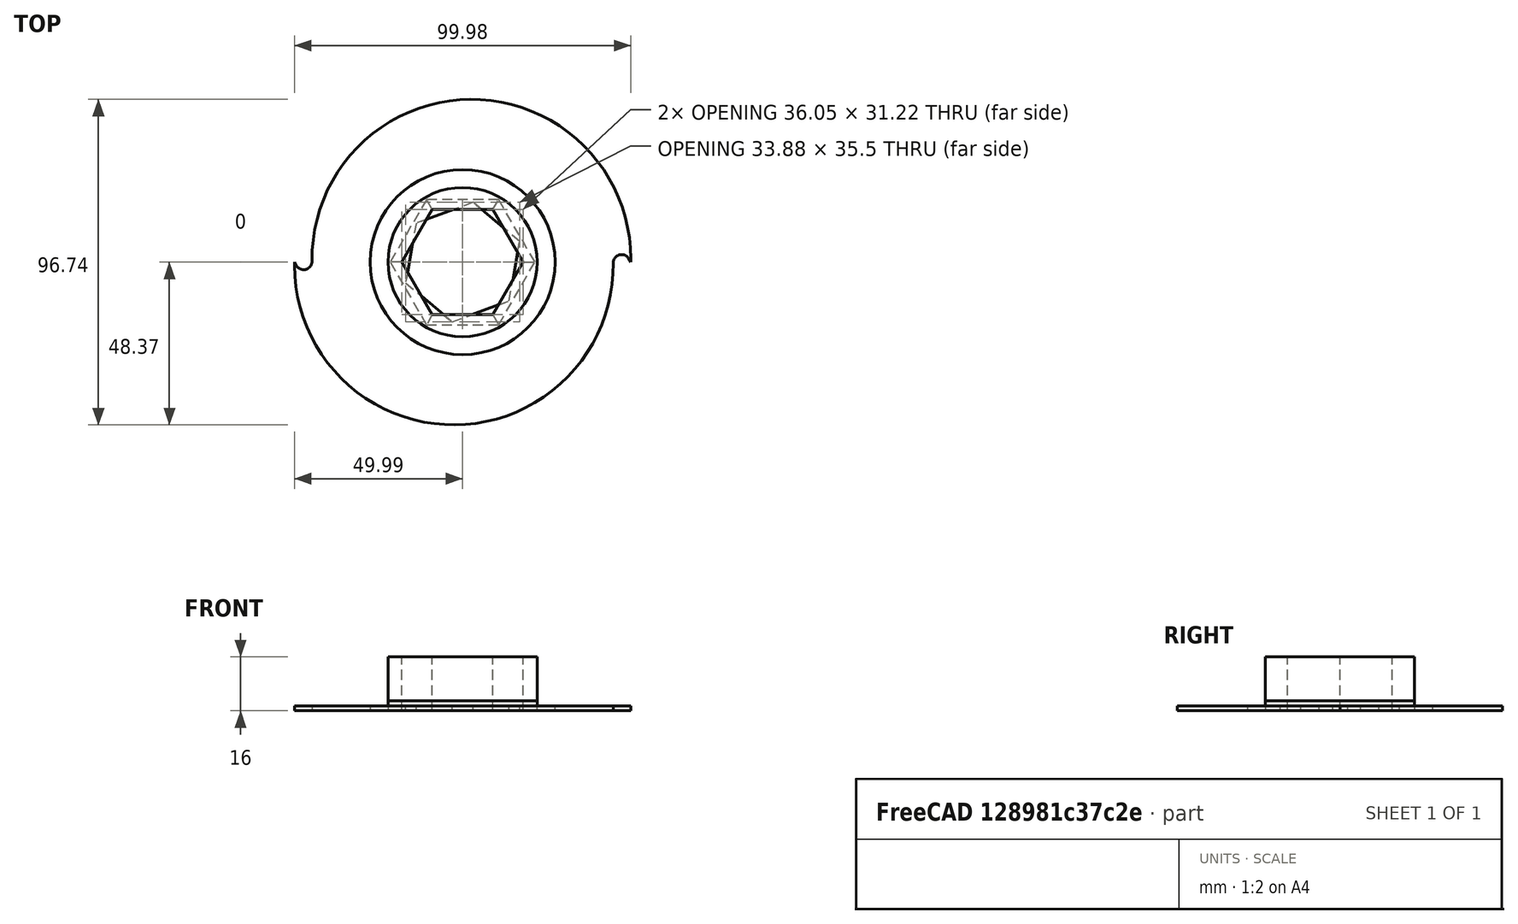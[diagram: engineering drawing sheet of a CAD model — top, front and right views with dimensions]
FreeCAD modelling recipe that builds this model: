
FCSTD DOCUMENT  (FreeCAD 0.21R33675 (Git))
Label: recicladora_cuchillas
License: All rights reserved
LicenseURL: https://en.wikipedia.org/wiki/All_rights_reserved
objects: Sketcher::SketchObject×21, PartDesign::CoordinateSystem×18, TechDraw::DrawViewDimension×13, PartDesign::Pad×9, PartDesign::Body×9, TechDraw::DrawProjGroupItem×8, TechDraw::DrawProjGroup×7, App::FeaturePython×1, PartDesign::Chamfer×1, TechDraw::DrawSVGTemplate×1, TechDraw::DrawPage×1
note: 74 computed .brp shape members not serialized (recipe doc carries the construction recipe); baked Part::Feature solids carry a one-line shape summary decoded from their .brp

FEATURE [Sketcher::SketchObject] Sketch001
  FullyConstrained = true
  MapMode = 5
  Support = -> [XY_Plane001]
  expr: Constraints[0] = dd.ddDiamteroExterno
  expr: Constraints[13] = dd.ddLargoPunta
  expr: Constraints[14] = dd.ddRadioMenor
  expr: Constraints[33] = dd.ddDistanceHexagono
  expr: Constraints[36] = dd.ddAngulo1
  expr: Constraints[8] = dd.ddAnguloPunta
  expr: Constraints[9] = dd.ddAnguloPunta
  sketch-geometry (17):
    g0: Circle CenterX=0 CenterY=0 CenterZ=0 NormalX=0 NormalY=0 NormalZ=1 AngleXU=0 Radius=50
    g1: LineSegment StartX=49.99 StartY=0 StartZ=0 EndX=49.99 EndY=1 EndZ=0
    g2: LineSegment StartX=49.99 StartY=0 StartZ=0 EndX=49.4126 EndY=1 EndZ=0
    g3: ArcOfCircle CenterX=2.61839 CenterY=1 CenterZ=0 NormalX=0 NormalY=0 NormalZ=1 AngleXU=0 Radius=47.3716 StartAngle=0 EndAngle=3.15663
    g4: ArcOfCircle CenterX=-2.61839 CenterY=-1 CenterZ=0 NormalX=0 NormalY=0 NormalZ=1 AngleXU=0 Radius=47.3716 StartAngle=3.14159 EndAngle=6.29822
    g5: LineSegment StartX=-49.99 StartY=0 StartZ=0 EndX=-49.99 EndY=-1 EndZ=0
    g6: LineSegment StartX=-49.99 StartY=0 StartZ=0 EndX=-49.4126 EndY=-1 EndZ=0
    g7: ArcOfCircle CenterX=-47.2476 CenterY=0.25 CenterZ=0 NormalX=0 NormalY=0 NormalZ=1 AngleXU=0 Radius=2.5 StartAngle=3.66519 EndAngle=6.29822
    g8: ArcOfCircle CenterX=47.2476 CenterY=-0.25 CenterZ=0 NormalX=0 NormalY=0 NormalZ=1 AngleXU=0 Radius=2.5 StartAngle=0.523599 EndAngle=3.15663
    g9: LineSegment StartX=-9.01244 StartY=-15.61 StartZ=0 EndX=9.01244 EndY=-15.61 EndZ=0
    g10: LineSegment StartX=9.01244 StartY=-15.61 StartZ=0 EndX=18.0249 EndY=0 EndZ=0
    g11: LineSegment StartX=18.0249 StartY=0 StartZ=0 EndX=9.01244 EndY=15.61 EndZ=0
    g12: LineSegment StartX=9.01244 StartY=15.61 StartZ=0 EndX=-9.01244 EndY=15.61 EndZ=0
    g13: LineSegment StartX=-9.01244 StartY=15.61 StartZ=0 EndX=-18.0249 EndY=1.8e-15 EndZ=0
    g14: LineSegment StartX=-18.0249 StartY=2e-15 StartZ=0 EndX=-9.01244 EndY=-15.61 EndZ=0
    g15: Circle CenterX=0 CenterY=0 CenterZ=0 NormalX=0 NormalY=0 NormalZ=1 AngleXU=0 Radius=18.0249
    g16: LineSegment StartX=0 StartY=0 StartZ=0 EndX=18.0249 EndY=0 EndZ=0
  constraints (42):
    c: Diameter(g0) = 100
    c: Tangent(g3,g1) = -1.5708
    c: Coincident(g6,g5)
    c: Tangent(g7,g6) = -1.5708
    c: Tangent(g7,g3) = 1.5708
    c: Tangent(g8,g2) = -1.5708
    c: Tangent(g8,g4) = 1.5708
    c: Coincident(g0,g-1)
    c: Angle(g1,g2) = 0.523599
    c: Angle(g5,g6) = 0.523599
    c: PointOnObject(g4,g0)
    c: Equal(g7,g8)
    c: Equal(g3,g4)
    c: Distance(g1) = 1
    c: Radius(g8) = 2.5
    c: Coincident(g9,g10)
    c: Coincident(g10,g11)
    c: Coincident(g11,g12)
    c: Coincident(g12,g13)
    c: Coincident(g13,g14)
    c: Coincident(g14,g9)
    c: Equal(g9, g10-g14) x5
    c: PointOnObject(g9,g15)
    c: PointOnObject(g10,g15)
    c: PointOnObject(g11,g15)
    c: PointOnObject(g12,g15)
    c: PointOnObject(g13,g15)
    c: PointOnObject(g14,g15)
    c: Coincident(g15,g0)
    c: Distance(g9,g10) = 31.22
    c: Coincident(g16,g0)
    c: Coincident(g16,g10)
    c: Angle(g-1,g16) = 0
    c: Tangent(g4,g5) = -1.5708
    c: Vertical(g1)
    c: Coincident(g1,g2)
    c: PointOnObject(g1,g0)
    c: PointOnObject(g1,g-1)
    c: Horizontal(g2,g1)
    c: Vertical(g5)
    c: PointOnObject(g5,g-1)
    c: Horizontal(g6,g4)
FEATURE [App::FeaturePython] dd  label="ddCuchillas"  # WARN: FeaturePython — macro-defined, semantics opaque (R4)
  DynamicData = Created with DynamicData (v2.46) workbench. | This is a simple container object built | for holding custom properties.
  ddAngulo1 = 0
  ddAngulo2 = 10
  ddAngulo3 = 20
  ddAngulo4 = 30
  ddAngulo5 = 40
  ddAngulo6 = 50
  ddAnguloPunta = 30
  ddDiametroSeparador = 55
  ddDiamteroExterno = 100
  ddDistanceHexagono = 31.22
  ddGrosorPlaca = 1.5
  ddLargoPunta = 1
  ddRadioMenor = 2.5
  expr: ddRadioMenor = 2.5
FEATURE [PartDesign::Pad] Pad001
  Direction = (0,0,1)
  Length = 1.5
  Length2 = 10
  Profile = -> Sketch001
  Type = 0
  expr: Length = <<ddCuchillas>>.ddGrosorPlaca
FEATURE [Sketcher::SketchObject] Sketch
  FullyConstrained = true
  MapMode = 5
  Placement = pos=(0,0,1.5) rot=(0,0,1;0rad)
  Support = -> [Pad001]
  expr: Constraints[0] = Sketch001.Constraints[0]
  expr: Constraints[14] = Sketch001.Constraints[8]
  expr: Constraints[15] = Sketch001.Constraints[9]
  expr: Constraints[21] = Sketch001.Constraints[13]
  expr: Constraints[22] = Sketch001.Constraints[14]
  expr: Constraints[41] = Sketch001.Constraints[33]
  expr: Constraints[44] = Sketch001.Constraints[36]
  sketch-geometry (17):
    g0: Circle CenterX=0 CenterY=0 CenterZ=0 NormalX=0 NormalY=0 NormalZ=1 AngleXU=0 Radius=50
    g1: LineSegment StartX=50 StartY=0 StartZ=0 EndX=49.99 EndY=0.99995 EndZ=0
    g2: LineSegment StartX=50 StartY=0 StartZ=0 EndX=49.4914 EndY=0.860982 EndZ=0
    g3: ArcOfCircle CenterX=2.57666 CenterY=0.525793 CenterZ=0 NormalX=0 NormalY=0 NormalZ=1 AngleXU=0 Radius=47.4157 StartAngle=0.0100002 EndAngle=3.1439
    g4: ArcOfCircle CenterX=-2.57666 CenterY=-0.525793 CenterZ=0 NormalX=0 NormalY=0 NormalZ=1 AngleXU=0 Radius=47.4157 StartAngle=3.15159 EndAngle=6.28549
    g5: LineSegment StartX=-50 StartY=0 StartZ=0 EndX=-49.99 EndY=-0.99995 EndZ=0
    g6: LineSegment StartX=-50 StartY=0 StartZ=0 EndX=-49.4914 EndY=-0.860982 EndZ=0
    g7: ArcOfCircle CenterX=-47.3389 CenterY=0.410606 CenterZ=0 NormalX=0 NormalY=0 NormalZ=1 AngleXU=0 Radius=2.5 StartAngle=3.67519 EndAngle=6.28549
    g8: ArcOfCircle CenterX=47.3389 CenterY=-0.410606 CenterZ=0 NormalX=0 NormalY=0 NormalZ=1 AngleXU=0 Radius=2.5 StartAngle=0.533599 EndAngle=3.1439
    g9: LineSegment StartX=-9.01244 StartY=-15.61 StartZ=0 EndX=9.01244 EndY=-15.61 EndZ=0
    g10: LineSegment StartX=9.01244 StartY=-15.61 StartZ=0 EndX=18.0249 EndY=0 EndZ=0
    g11: LineSegment StartX=18.0249 StartY=0 StartZ=0 EndX=9.01244 EndY=15.61 EndZ=0
    g12: LineSegment StartX=9.01244 StartY=15.61 StartZ=0 EndX=-9.01244 EndY=15.61 EndZ=0
    g13: LineSegment StartX=-9.01244 StartY=15.61 StartZ=0 EndX=-18.0249 EndY=0 EndZ=0
    g14: LineSegment StartX=-18.0249 StartY=7e-16 StartZ=0 EndX=-9.01244 EndY=-15.61 EndZ=0
    g15: Circle CenterX=0 CenterY=0 CenterZ=0 NormalX=0 NormalY=0 NormalZ=1 AngleXU=0 Radius=18.0249
    g16: LineSegment StartX=0 StartY=0 StartZ=0 EndX=18.0249 EndY=0 EndZ=0
  constraints (42):
    c: Diameter(g0) = 100
    c: PointOnObject(g1,g0)
    c: Coincident(g2,g1)
    c: PointOnObject(g1,g-1)
    c: Tangent(g3,g1) = -1.5708
    c: PointOnObject(g5,g-1)
    c: Coincident(g6,g5)
    c: Tangent(g7,g6) = -1.5708
    c: Tangent(g7,g3) = 1.5708
    c: Tangent(g8,g2) = -1.5708
    c: Tangent(g8,g4) = 1.5708
    c: PointOnObject(g5,g0)
    c: Coincident(g0,g-1)
    c: PointOnObject(g1,g0)
    c: Angle(g1,g2) = 0.523599
    c: Angle(g5,g6) = 0.523599
    c: Equal(g5,g1)
    c: PointOnObject(g4,g0)
    c: Equal(g7,g8)
    c: Equal(g3,g4)
    c: Equal(g5,g6)
    c: Distance(g1) = 1
    c: Radius(g8) = 2.5
    c: Coincident(g9,g10)
    c: Coincident(g10,g11)
    c: Coincident(g11,g12)
    c: Coincident(g12,g13)
    c: Coincident(g13,g14)
    c: Coincident(g14,g9)
    c: Equal(g9, g10-g14) x5
    c: PointOnObject(g9,g15)
    c: PointOnObject(g10,g15)
    c: PointOnObject(g11,g15)
    c: PointOnObject(g12,g15)
    c: PointOnObject(g13,g15)
    c: PointOnObject(g14,g15)
    c: Coincident(g15,g0)
    c: Distance(g9,g10) = 31.22
    c: Coincident(g16,g0)
    c: Coincident(g16,g10)
    c: Angle(g-1,g16) = 0
    c: Tangent(g4,g5) = -1.5708
FEATURE [Sketcher::SketchObject] Sketch002
  FullyConstrained = true
  MapMode = 5
  Placement = pos=(0,0,0) rot=(1,0,0;3.14159rad)
  Support = -> [Pad001]
  expr: Constraints[0] = Sketch.Constraints[0]
  expr: Constraints[14] = Sketch.Constraints[14]
  expr: Constraints[15] = Sketch.Constraints[15]
  expr: Constraints[21] = Sketch.Constraints[21]
  expr: Constraints[22] = Sketch.Constraints[22]
  expr: Constraints[41] = Sketch.Constraints[41]
  expr: Constraints[44] = Sketch.Constraints[44]
  sketch-geometry (17):
    g0: Circle CenterX=0 CenterY=0 CenterZ=0 NormalX=0 NormalY=0 NormalZ=1 AngleXU=0 Radius=50
    g1: LineSegment StartX=50 StartY=0 StartZ=0 EndX=49.99 EndY=0.99995 EndZ=0
    g2: LineSegment StartX=50 StartY=0 StartZ=0 EndX=49.4914 EndY=0.860982 EndZ=0
    g3: ArcOfCircle CenterX=2.57666 CenterY=0.525793 CenterZ=0 NormalX=0 NormalY=0 NormalZ=1 AngleXU=0 Radius=47.4157 StartAngle=0.0100002 EndAngle=3.1439
    g4: ArcOfCircle CenterX=-2.57666 CenterY=-0.525793 CenterZ=0 NormalX=0 NormalY=0 NormalZ=1 AngleXU=0 Radius=47.4157 StartAngle=3.15159 EndAngle=6.28549
    g5: LineSegment StartX=-50 StartY=0 StartZ=0 EndX=-49.99 EndY=-0.99995 EndZ=0
    g6: LineSegment StartX=-50 StartY=0 StartZ=0 EndX=-49.4914 EndY=-0.860982 EndZ=0
    g7: ArcOfCircle CenterX=-47.3389 CenterY=0.410606 CenterZ=0 NormalX=0 NormalY=0 NormalZ=1 AngleXU=0 Radius=2.5 StartAngle=3.67519 EndAngle=6.28549
    g8: ArcOfCircle CenterX=47.3389 CenterY=-0.410606 CenterZ=0 NormalX=0 NormalY=0 NormalZ=1 AngleXU=0 Radius=2.5 StartAngle=0.533599 EndAngle=3.1439
    g9: LineSegment StartX=-9.01244 StartY=-15.61 StartZ=0 EndX=9.01244 EndY=-15.61 EndZ=0
    g10: LineSegment StartX=9.01244 StartY=-15.61 StartZ=0 EndX=18.0249 EndY=0 EndZ=0
    g11: LineSegment StartX=18.0249 StartY=0 StartZ=0 EndX=9.01244 EndY=15.61 EndZ=0
    g12: LineSegment StartX=9.01244 StartY=15.61 StartZ=0 EndX=-9.01244 EndY=15.61 EndZ=0
    g13: LineSegment StartX=-9.01244 StartY=15.61 StartZ=0 EndX=-18.0249 EndY=1.8e-15 EndZ=0
    g14: LineSegment StartX=-18.0249 StartY=2.1e-15 StartZ=0 EndX=-9.01244 EndY=-15.61 EndZ=0
    g15: Circle CenterX=0 CenterY=0 CenterZ=0 NormalX=0 NormalY=0 NormalZ=1 AngleXU=0 Radius=18.0249
    g16: LineSegment StartX=0 StartY=0 StartZ=0 EndX=18.0249 EndY=0 EndZ=0
  constraints (42):
    c: Diameter(g0) = 100
    c: PointOnObject(g1,g0)
    c: Coincident(g2,g1)
    c: PointOnObject(g1,g-1)
    c: Tangent(g3,g1) = -1.5708
    c: PointOnObject(g5,g-1)
    c: Coincident(g6,g5)
    c: Tangent(g7,g6) = -1.5708
    c: Tangent(g7,g3) = 1.5708
    c: Tangent(g8,g2) = -1.5708
    c: Tangent(g8,g4) = 1.5708
    c: PointOnObject(g5,g0)
    c: Coincident(g0,g-1)
    c: PointOnObject(g1,g0)
    c: Angle(g1,g2) = 0.523599
    c: Angle(g5,g6) = 0.523599
    c: Equal(g5,g1)
    c: PointOnObject(g4,g0)
    c: Equal(g7,g8)
    c: Equal(g3,g4)
    c: Equal(g5,g6)
    c: Distance(g1) = 1
    c: Radius(g8) = 2.5
    c: Coincident(g9,g10)
    c: Coincident(g10,g11)
    c: Coincident(g11,g12)
    c: Coincident(g12,g13)
    c: Coincident(g13,g14)
    c: Coincident(g14,g9)
    c: Equal(g9, g10-g14) x5
    c: PointOnObject(g9,g15)
    c: PointOnObject(g10,g15)
    c: PointOnObject(g11,g15)
    c: PointOnObject(g12,g15)
    c: PointOnObject(g13,g15)
    c: PointOnObject(g14,g15)
    c: Coincident(g15,g0)
    c: Distance(g9,g10) = 31.22
    c: Coincident(g16,g0)
    c: Coincident(g16,g10)
    c: Angle(g-1,g16) = 0
    c: Tangent(g4,g5) = -1.5708
FEATURE [PartDesign::CoordinateSystem] LCS_cuchilla_entrada
  AttacherType = Attacher::AttachEngine3D
  MapMode = 11
  Placement = pos=(-3.6e-15,0,0) rot=(0,0,1;1.5708rad)
  Support = -> [Sketch002,Pad001]
FEATURE [PartDesign::CoordinateSystem] LCS_cuchilla_salida
  AttacherType = Attacher::AttachEngine3D
  MapMode = 11
  Placement = pos=(-3.6e-15,0,1.5) rot=(0,0,1;1.5708rad)
  Support = -> [Sketch,Pad001]
FEATURE [PartDesign::Body] Body001  label="Cuchilla001"
  Group = -> [Sketch001,Pad001,LCS_cuchilla_entrada,Sketch,Sketch002,LCS_cuchilla_salida]
  Origin = -> Origin001
  Tip = -> Pad001
FEATURE [Sketcher::SketchObject] Sketch018
  FullyConstrained = true
  MapMode = 5
  Support = -> [XY_Plane001]
  expr: Constraints[19] = 22.18 * 2
  expr: Constraints[20] = dd.ddDistanceHexagono
  sketch-geometry (8):
    g0: LineSegment StartX=9.01244 StartY=15.61 StartZ=0 EndX=-9.01244 EndY=15.61 EndZ=0
    g1: LineSegment StartX=-9.01244 StartY=15.61 StartZ=0 EndX=-18.0249 EndY=-1.8e-15 EndZ=0
    g2: LineSegment StartX=-18.0249 StartY=-1.8e-15 StartZ=0 EndX=-9.01244 EndY=-15.61 EndZ=0
    g3: LineSegment StartX=-9.01244 StartY=-15.61 StartZ=0 EndX=9.01244 EndY=-15.61 EndZ=0
    g4: LineSegment StartX=9.01244 StartY=-15.61 StartZ=0 EndX=18.0249 EndY=0 EndZ=0
    g5: LineSegment StartX=18.0249 StartY=0 StartZ=0 EndX=9.01244 EndY=15.61 EndZ=0
    g6: Circle CenterX=0 CenterY=0 CenterZ=0 NormalX=0 NormalY=0 NormalZ=1 AngleXU=0 Radius=18.0249
    g7: Circle CenterX=0 CenterY=0 CenterZ=0 NormalX=0 NormalY=0 NormalZ=1 AngleXU=0 Radius=22.18
  constraints (18):
    c: Coincident(g0,g1)
    c: Coincident(g1,g2)
    c: Coincident(g2,g3)
    c: Coincident(g3,g4)
    c: Coincident(g4,g5)
    c: Coincident(g5,g0)
    c: Equal(g0, g1-g5) x5
    c: PointOnObject(g0,g6)
    c: PointOnObject(g1,g6)
    c: PointOnObject(g2,g6)
    c: PointOnObject(g3,g6)
    c: PointOnObject(g4,g6)
    c: PointOnObject(g5,g6)
    c: Coincident(g6,g-1)
    c: Coincident(g7,g6)
    c: Diameter(g7) = 44.36
    c: Distance(g1,g0) = 31.22
    c: PointOnObject(g4,g-1)
FEATURE [PartDesign::Pad] Pad007
  Direction = (0,0,1)
  Length = 3
  Length2 = 10
  Profile = -> Sketch018
  Type = 0
FEATURE [PartDesign::Chamfer] Chamfer
  Angle = 45
  Base = -> Pad007 [Edge15,Edge18,Edge20,Edge6,Edge9,Edge12]
  BaseFeature = -> Pad007
  ChamferType = 0
  FlipDirection = false
  Size = 2.9999
  Size2 = 1
  SupportTransform = false
  UseAllEdges = false
  expr: Size = 3 mm - 0.0001 mm
FEATURE [PartDesign::CoordinateSystem] LCS_separador_entrada  label="LCS_separador_inicial_entrada"
  AttacherType = Attacher::AttachEngine3D
  MapMode = 11
  Placement = pos=(-3.6e-15,0,0) rot=(0,0,1;1.5708rad)
  Support = -> [Chamfer]
FEATURE [PartDesign::CoordinateSystem] LCS_separador_inicial_salida
  AttacherType = Attacher::AttachEngine3D
  MapMode = 11
  Placement = pos=(-3.6e-15,0,3) rot=(0,0,1;1.5708rad)
  Support = -> [Chamfer]
FEATURE [PartDesign::Body] Body007  label="SeparadorCuchillaInicial"
  Group = -> [Sketch018,Pad007,Chamfer,LCS_separador_entrada,LCS_separador_inicial_salida]
  Origin = -> Origin007
  Tip = -> Chamfer
FEATURE [Sketcher::SketchObject] Sketch019
  FullyConstrained = true
  MapMode = 5
  Support = -> [XY_Plane001]
  expr: Constraints[19] = <<ddCuchillas>>.ddDiametroSeparador
  expr: Constraints[21] = dd.ddDistanceHexagono
  sketch-geometry (8):
    g0: LineSegment StartX=9.01244 StartY=15.61 StartZ=0 EndX=-9.01244 EndY=15.61 EndZ=0
    g1: LineSegment StartX=-9.01244 StartY=15.61 StartZ=0 EndX=-18.0249 EndY=3.6e-15 EndZ=0
    g2: LineSegment StartX=-18.0249 StartY=3.6e-15 StartZ=0 EndX=-9.01244 EndY=-15.61 EndZ=0
    g3: LineSegment StartX=-9.01244 StartY=-15.61 StartZ=0 EndX=9.01244 EndY=-15.61 EndZ=0
    g4: LineSegment StartX=9.01244 StartY=-15.61 StartZ=0 EndX=18.0249 EndY=0 EndZ=0
    g5: LineSegment StartX=18.0249 StartY=0 StartZ=0 EndX=9.01244 EndY=15.61 EndZ=0
    g6: Circle CenterX=0 CenterY=0 CenterZ=0 NormalX=0 NormalY=0 NormalZ=1 AngleXU=0 Radius=18.0249
    g7: Circle CenterX=0 CenterY=0 CenterZ=0 NormalX=0 NormalY=0 NormalZ=1 AngleXU=0 Radius=27.5
  constraints (18):
    c: Coincident(g0,g1)
    c: Coincident(g1,g2)
    c: Coincident(g2,g3)
    c: Coincident(g3,g4)
    c: Coincident(g4,g5)
    c: Coincident(g5,g0)
    c: Equal(g0, g1-g5) x5
    c: PointOnObject(g0,g6)
    c: PointOnObject(g1,g6)
    c: PointOnObject(g2,g6)
    c: PointOnObject(g3,g6)
    c: PointOnObject(g4,g6)
    c: PointOnObject(g5,g6)
    c: Coincident(g6,g-1)
    c: Coincident(g7,g6)
    c: Diameter(g7) = 55
    c: PointOnObject(g4,g-1)
    c: Distance(g0,g1) = 31.22
FEATURE [PartDesign::Pad] Pad008
  Direction = (0,0,1)
  Length = 1.5
  Length2 = 10
  Profile = -> Sketch019
  Type = 0
  expr: Length = dd.ddGrosorPlaca
FEATURE [PartDesign::CoordinateSystem] LCS_separador  label="LCS_separador_entrada"
  AttacherType = Attacher::AttachEngine3D
  MapMode = 11
  Placement = pos=(0,0,1.5) rot=(0.707107,-0.707107,0;3.14159rad)
  Support = -> [Pad008]
FEATURE [PartDesign::CoordinateSystem] LCS_separador_salida
  AttacherType = Attacher::AttachEngine3D
  MapMode = 11
  Placement = pos=(0,0,0) rot=(0.707107,-0.707107,0;3.14159rad)
  Support = -> [Pad008]
FEATURE [PartDesign::Body] Body008  label="SeparadorCuchilla"
  Group = -> [Sketch019,Pad008,LCS_separador,LCS_separador_salida]
  Origin = -> Origin008
  Tip = -> Pad008
FEATURE [Sketcher::SketchObject] Sketch021
  FullyConstrained = true
  MapMode = 5
  Support = -> [XY_Plane002]
  expr: Constraints[0] = dd.ddDiamteroExterno
  expr: Constraints[13] = dd.ddLargoPunta
  expr: Constraints[14] = dd.ddRadioMenor
  expr: Constraints[33] = dd.ddDistanceHexagono
  expr: Constraints[36] = dd.ddAngulo2
  expr: Constraints[8] = dd.ddAnguloPunta
  expr: Constraints[9] = dd.ddAnguloPunta
  sketch-geometry (17):
    g0: Circle CenterX=0 CenterY=0 CenterZ=0 NormalX=0 NormalY=0 NormalZ=1 AngleXU=0 Radius=50
    g1: LineSegment StartX=49.99 StartY=0 StartZ=0 EndX=49.99 EndY=1 EndZ=0
    g2: LineSegment StartX=49.99 StartY=0 StartZ=0 EndX=49.4126 EndY=1 EndZ=0
    g3: ArcOfCircle CenterX=2.61839 CenterY=1 CenterZ=0 NormalX=0 NormalY=0 NormalZ=1 AngleXU=0 Radius=47.3716 StartAngle=0 EndAngle=3.15663
    g4: ArcOfCircle CenterX=-2.61839 CenterY=-1 CenterZ=0 NormalX=0 NormalY=0 NormalZ=1 AngleXU=0 Radius=47.3716 StartAngle=3.14159 EndAngle=6.29822
    g5: LineSegment StartX=-49.99 StartY=0 StartZ=0 EndX=-49.99 EndY=-1 EndZ=0
    g6: LineSegment StartX=-49.99 StartY=0 StartZ=0 EndX=-49.4126 EndY=-1 EndZ=0
    g7: ArcOfCircle CenterX=-47.2476 CenterY=0.25 CenterZ=0 NormalX=0 NormalY=0 NormalZ=1 AngleXU=0 Radius=2.5 StartAngle=3.66519 EndAngle=6.29822
    g8: ArcOfCircle CenterX=47.2476 CenterY=-0.25 CenterZ=0 NormalX=0 NormalY=0 NormalZ=1 AngleXU=0 Radius=2.5 StartAngle=0.523599 EndAngle=3.15663
    g9: LineSegment StartX=-6.16487 StartY=-16.9378 StartZ=0 EndX=11.5862 EndY=-13.8079 EndZ=0
    g10: LineSegment StartX=11.5862 StartY=-13.8079 StartZ=0 EndX=17.751 EndY=3.12999 EndZ=0
    g11: LineSegment StartX=17.751 StartY=3.12999 StartZ=0 EndX=6.16487 EndY=16.9378 EndZ=0
    g12: LineSegment StartX=6.16487 StartY=16.9378 StartZ=0 EndX=-11.5862 EndY=13.8079 EndZ=0
    g13: LineSegment StartX=-11.5862 StartY=13.8079 StartZ=0 EndX=-17.751 EndY=-3.12999 EndZ=0
    g14: LineSegment StartX=-17.751 StartY=-3.12999 StartZ=0 EndX=-6.16487 EndY=-16.9378 EndZ=0
    g15: Circle CenterX=0 CenterY=0 CenterZ=0 NormalX=0 NormalY=0 NormalZ=1 AngleXU=0 Radius=18.0249
    g16: LineSegment StartX=0 StartY=0 StartZ=0 EndX=17.751 EndY=3.12999 EndZ=0
  constraints (42):
    c: Diameter(g0) = 100
    c: Tangent(g3,g1) = -1.5708
    c: Coincident(g6,g5)
    c: Tangent(g7,g6) = -1.5708
    c: Tangent(g7,g3) = 1.5708
    c: Tangent(g8,g2) = -1.5708
    c: Tangent(g8,g4) = 1.5708
    c: Coincident(g0,g-1)
    c: Angle(g1,g2) = 0.523599
    c: Angle(g5,g6) = 0.523599
    c: PointOnObject(g4,g0)
    c: Equal(g7,g8)
    c: Equal(g3,g4)
    c: Distance(g1) = 1
    c: Radius(g8) = 2.5
    c: Coincident(g9,g10)
    c: Coincident(g10,g11)
    c: Coincident(g11,g12)
    c: Coincident(g12,g13)
    c: Coincident(g13,g14)
    c: Coincident(g14,g9)
    c: Equal(g9, g10-g14) x5
    c: PointOnObject(g9,g15)
    c: PointOnObject(g10,g15)
    c: PointOnObject(g11,g15)
    c: PointOnObject(g12,g15)
    c: PointOnObject(g13,g15)
    c: PointOnObject(g14,g15)
    c: Coincident(g15,g0)
    c: Distance(g9,g10) = 31.22
    c: Coincident(g16,g0)
    c: Coincident(g16,g10)
    c: Angle(g-1,g16) = 0.174533
    c: Tangent(g4,g5) = -1.5708
    c: Vertical(g1)
    c: Coincident(g1,g2)
    c: PointOnObject(g1,g0)
    c: PointOnObject(g1,g-1)
    c: Horizontal(g2,g1)
    c: Vertical(g5)
    c: PointOnObject(g5,g-1)
    c: Horizontal(g6,g4)
FEATURE [PartDesign::Pad] Pad009
  Direction = (0,0,1)
  Length = 1.5
  Length2 = 10
  Profile = -> Sketch021
  Type = 0
  expr: Length = <<ddCuchillas>>.ddGrosorPlaca
FEATURE [Sketcher::SketchObject] Sketch020
  FullyConstrained = true
  MapMode = 5
  Placement = pos=(0,0,1.5) rot=(0,0,1;0rad)
  Support = -> [Pad009]
  expr: Constraints[0] = Sketch021.Constraints[0]
  expr: Constraints[14] = Sketch021.Constraints[8]
  expr: Constraints[15] = Sketch021.Constraints[9]
  expr: Constraints[21] = Sketch021.Constraints[13]
  expr: Constraints[22] = Sketch021.Constraints[14]
  expr: Constraints[41] = Sketch021.Constraints[33]
  expr: Constraints[44] = Sketch021.Constraints[36]
  sketch-geometry (17):
    g0: Circle CenterX=0 CenterY=0 CenterZ=0 NormalX=0 NormalY=0 NormalZ=1 AngleXU=0 Radius=50
    g1: LineSegment StartX=50 StartY=0 StartZ=0 EndX=49.99 EndY=0.99995 EndZ=0
    g2: LineSegment StartX=50 StartY=0 StartZ=0 EndX=49.4914 EndY=0.860982 EndZ=0
    g3: ArcOfCircle CenterX=2.57666 CenterY=0.525793 CenterZ=0 NormalX=0 NormalY=0 NormalZ=1 AngleXU=0 Radius=47.4157 StartAngle=0.0100002 EndAngle=3.1439
    g4: ArcOfCircle CenterX=-2.57666 CenterY=-0.525793 CenterZ=0 NormalX=0 NormalY=0 NormalZ=1 AngleXU=0 Radius=47.4157 StartAngle=3.15159 EndAngle=6.28549
    g5: LineSegment StartX=-50 StartY=0 StartZ=0 EndX=-49.99 EndY=-0.99995 EndZ=0
    g6: LineSegment StartX=-50 StartY=0 StartZ=0 EndX=-49.4914 EndY=-0.860982 EndZ=0
    g7: ArcOfCircle CenterX=-47.3389 CenterY=0.410606 CenterZ=0 NormalX=0 NormalY=0 NormalZ=1 AngleXU=0 Radius=2.5 StartAngle=3.67519 EndAngle=6.28549
    g8: ArcOfCircle CenterX=47.3389 CenterY=-0.410606 CenterZ=0 NormalX=0 NormalY=0 NormalZ=1 AngleXU=0 Radius=2.5 StartAngle=0.533599 EndAngle=3.1439
    g9: LineSegment StartX=-6.16487 StartY=-16.9378 StartZ=0 EndX=11.5862 EndY=-13.8079 EndZ=0
    g10: LineSegment StartX=11.5862 StartY=-13.8079 StartZ=0 EndX=17.751 EndY=3.12999 EndZ=0
    g11: LineSegment StartX=17.751 StartY=3.12999 StartZ=0 EndX=6.16487 EndY=16.9378 EndZ=0
    g12: LineSegment StartX=6.16487 StartY=16.9378 StartZ=0 EndX=-11.5862 EndY=13.8079 EndZ=0
    g13: LineSegment StartX=-11.5862 StartY=13.8079 StartZ=0 EndX=-17.751 EndY=-3.12999 EndZ=0
    g14: LineSegment StartX=-17.751 StartY=-3.12999 StartZ=0 EndX=-6.16487 EndY=-16.9378 EndZ=0
    g15: Circle CenterX=0 CenterY=0 CenterZ=0 NormalX=0 NormalY=0 NormalZ=1 AngleXU=0 Radius=18.0249
    g16: LineSegment StartX=0 StartY=0 StartZ=0 EndX=17.751 EndY=3.12999 EndZ=0
  constraints (42):
    c: Diameter(g0) = 100
    c: PointOnObject(g1,g0)
    c: Coincident(g2,g1)
    c: PointOnObject(g1,g-1)
    c: Tangent(g3,g1) = -1.5708
    c: PointOnObject(g5,g-1)
    c: Coincident(g6,g5)
    c: Tangent(g7,g6) = -1.5708
    c: Tangent(g7,g3) = 1.5708
    c: Tangent(g8,g2) = -1.5708
    c: Tangent(g8,g4) = 1.5708
    c: PointOnObject(g5,g0)
    c: Coincident(g0,g-1)
    c: PointOnObject(g1,g0)
    c: Angle(g1,g2) = 0.523599
    c: Angle(g5,g6) = 0.523599
    c: Equal(g5,g1)
    c: PointOnObject(g4,g0)
    c: Equal(g7,g8)
    c: Equal(g3,g4)
    c: Equal(g5,g6)
    c: Distance(g1) = 1
    c: Radius(g8) = 2.5
    c: Coincident(g9,g10)
    c: Coincident(g10,g11)
    c: Coincident(g11,g12)
    c: Coincident(g12,g13)
    c: Coincident(g13,g14)
    c: Coincident(g14,g9)
    c: Equal(g9, g10-g14) x5
    c: PointOnObject(g9,g15)
    c: PointOnObject(g10,g15)
    c: PointOnObject(g11,g15)
    c: PointOnObject(g12,g15)
    c: PointOnObject(g13,g15)
    c: PointOnObject(g14,g15)
    c: Coincident(g15,g0)
    c: Distance(g9,g10) = 31.22
    c: Coincident(g16,g0)
    c: Coincident(g16,g10)
    c: Angle(g-1,g16) = 0.174533
    c: Tangent(g4,g5) = -1.5708
FEATURE [PartDesign::CoordinateSystem] LCS_cuchilla_salida001
  AttacherType = Attacher::AttachEngine3D
  MapMode = 11
  Placement = pos=(-3.6e-15,-4e-16,1.5) rot=(0,0,1;1.74533rad)
  Support = -> [Sketch020,Pad009]
FEATURE [Sketcher::SketchObject] Sketch022
  FullyConstrained = true
  MapMode = 5
  Placement = pos=(0,0,0) rot=(1,0,0;3.14159rad)
  Support = -> [Pad009]
  expr: Constraints[0] = Sketch020.Constraints[0]
  expr: Constraints[14] = Sketch020.Constraints[14]
  expr: Constraints[15] = Sketch020.Constraints[15]
  expr: Constraints[21] = Sketch020.Constraints[21]
  expr: Constraints[22] = Sketch020.Constraints[22]
  expr: Constraints[41] = Sketch020.Constraints[41]
  expr: Constraints[44] = Sketch020.Constraints[44]
  sketch-geometry (17):
    g0: Circle CenterX=0 CenterY=0 CenterZ=0 NormalX=0 NormalY=0 NormalZ=1 AngleXU=0 Radius=50
    g1: LineSegment StartX=50 StartY=0 StartZ=0 EndX=49.99 EndY=0.99995 EndZ=0
    g2: LineSegment StartX=50 StartY=0 StartZ=0 EndX=49.4914 EndY=0.860982 EndZ=0
    g3: ArcOfCircle CenterX=2.57666 CenterY=0.525793 CenterZ=0 NormalX=0 NormalY=0 NormalZ=1 AngleXU=0 Radius=47.4157 StartAngle=0.0100002 EndAngle=3.1439
    g4: ArcOfCircle CenterX=-2.57666 CenterY=-0.525793 CenterZ=0 NormalX=0 NormalY=0 NormalZ=1 AngleXU=0 Radius=47.4157 StartAngle=3.15159 EndAngle=6.28549
    g5: LineSegment StartX=-50 StartY=0 StartZ=0 EndX=-49.99 EndY=-0.99995 EndZ=0
    g6: LineSegment StartX=-50 StartY=0 StartZ=0 EndX=-49.4914 EndY=-0.860982 EndZ=0
    g7: ArcOfCircle CenterX=-47.3389 CenterY=0.410606 CenterZ=0 NormalX=0 NormalY=0 NormalZ=1 AngleXU=0 Radius=2.5 StartAngle=3.67519 EndAngle=6.28549
    g8: ArcOfCircle CenterX=47.3389 CenterY=-0.410606 CenterZ=0 NormalX=0 NormalY=0 NormalZ=1 AngleXU=0 Radius=2.5 StartAngle=0.533599 EndAngle=3.1439
    g9: LineSegment StartX=-6.16487 StartY=-16.9378 StartZ=0 EndX=11.5862 EndY=-13.8079 EndZ=0
    g10: LineSegment StartX=11.5862 StartY=-13.8079 StartZ=0 EndX=17.751 EndY=3.12999 EndZ=0
    g11: LineSegment StartX=17.751 StartY=3.12999 StartZ=0 EndX=6.16487 EndY=16.9378 EndZ=0
    g12: LineSegment StartX=6.16487 StartY=16.9378 StartZ=0 EndX=-11.5862 EndY=13.8079 EndZ=0
    g13: LineSegment StartX=-11.5862 StartY=13.8079 StartZ=0 EndX=-17.751 EndY=-3.12999 EndZ=0
    g14: LineSegment StartX=-17.751 StartY=-3.12999 StartZ=0 EndX=-6.16487 EndY=-16.9378 EndZ=0
    g15: Circle CenterX=0 CenterY=0 CenterZ=0 NormalX=0 NormalY=0 NormalZ=1 AngleXU=0 Radius=18.0249
    g16: LineSegment StartX=0 StartY=0 StartZ=0 EndX=17.751 EndY=3.12999 EndZ=0
  constraints (42):
    c: Diameter(g0) = 100
    c: PointOnObject(g1,g0)
    c: Coincident(g2,g1)
    c: PointOnObject(g1,g-1)
    c: Tangent(g3,g1) = -1.5708
    c: PointOnObject(g5,g-1)
    c: Coincident(g6,g5)
    c: Tangent(g7,g6) = -1.5708
    c: Tangent(g7,g3) = 1.5708
    c: Tangent(g8,g2) = -1.5708
    c: Tangent(g8,g4) = 1.5708
    c: PointOnObject(g5,g0)
    c: Coincident(g0,g-1)
    c: PointOnObject(g1,g0)
    c: Angle(g1,g2) = 0.523599
    c: Angle(g5,g6) = 0.523599
    c: Equal(g5,g1)
    c: PointOnObject(g4,g0)
    c: Equal(g7,g8)
    c: Equal(g3,g4)
    c: Equal(g5,g6)
    c: Distance(g1) = 1
    c: Radius(g8) = 2.5
    c: Coincident(g9,g10)
    c: Coincident(g10,g11)
    c: Coincident(g11,g12)
    c: Coincident(g12,g13)
    c: Coincident(g13,g14)
    c: Coincident(g14,g9)
    c: Equal(g9, g10-g14) x5
    c: PointOnObject(g9,g15)
    c: PointOnObject(g10,g15)
    c: PointOnObject(g11,g15)
    c: PointOnObject(g12,g15)
    c: PointOnObject(g13,g15)
    c: PointOnObject(g14,g15)
    c: Coincident(g15,g0)
    c: Distance(g9,g10) = 31.22
    c: Coincident(g16,g0)
    c: Coincident(g16,g10)
    c: Angle(g-1,g16) = 0.174533
    c: Tangent(g4,g5) = -1.5708
FEATURE [PartDesign::CoordinateSystem] LCS_cuchilla_entrada001
  AttacherType = Attacher::AttachEngine3D
  MapMode = 11
  Placement = pos=(-3.6e-15,-4e-16,0) rot=(0,0,1;1.74533rad)
  Support = -> [Sketch022,Pad009]
FEATURE [PartDesign::Body] Body009  label="Cuchilla002"
  Group = -> [Sketch021,Pad009,LCS_cuchilla_entrada001,Sketch020,Sketch022,LCS_cuchilla_salida001]
  Origin = -> Origin009
  Tip = -> Pad009
FEATURE [Sketcher::SketchObject] Sketch024
  FullyConstrained = true
  MapMode = 5
  Support = -> [XY_Plane003]
  expr: Constraints[0] = dd.ddDiamteroExterno
  expr: Constraints[13] = dd.ddLargoPunta
  expr: Constraints[14] = dd.ddRadioMenor
  expr: Constraints[33] = dd.ddDistanceHexagono
  expr: Constraints[36] = dd.ddAngulo3
  expr: Constraints[8] = dd.ddAnguloPunta
  expr: Constraints[9] = dd.ddAnguloPunta
  sketch-geometry (17):
    g0: Circle CenterX=0 CenterY=0 CenterZ=0 NormalX=0 NormalY=0 NormalZ=1 AngleXU=0 Radius=50
    g1: LineSegment StartX=49.99 StartY=0 StartZ=0 EndX=49.99 EndY=1 EndZ=0
    g2: LineSegment StartX=49.99 StartY=0 StartZ=0 EndX=49.4126 EndY=1 EndZ=0
    g3: ArcOfCircle CenterX=2.61839 CenterY=1 CenterZ=0 NormalX=0 NormalY=0 NormalZ=1 AngleXU=0 Radius=47.3716 StartAngle=0 EndAngle=3.15663
    g4: ArcOfCircle CenterX=-2.61839 CenterY=-1 CenterZ=0 NormalX=0 NormalY=0 NormalZ=1 AngleXU=0 Radius=47.3716 StartAngle=3.14159 EndAngle=6.29822
    g5: LineSegment StartX=-49.99 StartY=0 StartZ=0 EndX=-49.99 EndY=-1 EndZ=0
    g6: LineSegment StartX=-49.99 StartY=0 StartZ=0 EndX=-49.4126 EndY=-1 EndZ=0
    g7: ArcOfCircle CenterX=-47.2476 CenterY=0.25 CenterZ=0 NormalX=0 NormalY=0 NormalZ=1 AngleXU=0 Radius=2.5 StartAngle=3.66519 EndAngle=6.29822
    g8: ArcOfCircle CenterX=47.2476 CenterY=-0.25 CenterZ=0 NormalX=0 NormalY=0 NormalZ=1 AngleXU=0 Radius=2.5 StartAngle=0.523599 EndAngle=3.15663
    g9: LineSegment StartX=-3.12999 StartY=-17.751 StartZ=0 EndX=13.8079 EndY=-11.5862 EndZ=0
    g10: LineSegment StartX=13.8079 StartY=-11.5862 StartZ=0 EndX=16.9378 EndY=6.16487 EndZ=0
    g11: LineSegment StartX=16.9378 StartY=6.16487 StartZ=0 EndX=3.12999 EndY=17.751 EndZ=0
    g12: LineSegment StartX=3.12999 StartY=17.751 StartZ=0 EndX=-13.8079 EndY=11.5862 EndZ=0
    g13: LineSegment StartX=-13.8079 StartY=11.5862 StartZ=0 EndX=-16.9378 EndY=-6.16487 EndZ=0
    g14: LineSegment StartX=-16.9378 StartY=-6.16487 StartZ=0 EndX=-3.12999 EndY=-17.751 EndZ=0
    g15: Circle CenterX=0 CenterY=0 CenterZ=0 NormalX=0 NormalY=0 NormalZ=1 AngleXU=0 Radius=18.0249
    g16: LineSegment StartX=0 StartY=0 StartZ=0 EndX=16.9378 EndY=6.16487 EndZ=0
  constraints (42):
    c: Diameter(g0) = 100
    c: Tangent(g3,g1) = -1.5708
    c: Coincident(g6,g5)
    c: Tangent(g7,g6) = -1.5708
    c: Tangent(g7,g3) = 1.5708
    c: Tangent(g8,g2) = -1.5708
    c: Tangent(g8,g4) = 1.5708
    c: Coincident(g0,g-1)
    c: Angle(g1,g2) = 0.523599
    c: Angle(g5,g6) = 0.523599
    c: PointOnObject(g4,g0)
    c: Equal(g7,g8)
    c: Equal(g3,g4)
    c: Distance(g1) = 1
    c: Radius(g8) = 2.5
    c: Coincident(g9,g10)
    c: Coincident(g10,g11)
    c: Coincident(g11,g12)
    c: Coincident(g12,g13)
    c: Coincident(g13,g14)
    c: Coincident(g14,g9)
    c: Equal(g9, g10-g14) x5
    c: PointOnObject(g9,g15)
    c: PointOnObject(g10,g15)
    c: PointOnObject(g11,g15)
    c: PointOnObject(g12,g15)
    c: PointOnObject(g13,g15)
    c: PointOnObject(g14,g15)
    c: Coincident(g15,g0)
    c: Distance(g9,g10) = 31.22
    c: Coincident(g16,g0)
    c: Coincident(g16,g10)
    c: Angle(g-1,g16) = 0.349066
    c: Tangent(g4,g5) = -1.5708
    c: Vertical(g1)
    c: Coincident(g1,g2)
    c: PointOnObject(g1,g0)
    c: PointOnObject(g1,g-1)
    c: Horizontal(g2,g1)
    c: Vertical(g5)
    c: PointOnObject(g5,g-1)
    c: Horizontal(g6,g4)
FEATURE [PartDesign::Pad] Pad010
  Direction = (0,0,1)
  Length = 1.5
  Length2 = 10
  Profile = -> Sketch024
  Type = 0
  expr: Length = <<ddCuchillas>>.ddGrosorPlaca
FEATURE [Sketcher::SketchObject] Sketch023
  FullyConstrained = true
  MapMode = 5
  Placement = pos=(0,0,1.5) rot=(0,0,1;0rad)
  Support = -> [Pad010]
  expr: Constraints[0] = Sketch024.Constraints[0]
  expr: Constraints[14] = Sketch024.Constraints[8]
  expr: Constraints[15] = Sketch024.Constraints[9]
  expr: Constraints[21] = Sketch024.Constraints[13]
  expr: Constraints[22] = Sketch024.Constraints[14]
  expr: Constraints[41] = Sketch024.Constraints[33]
  expr: Constraints[44] = Sketch024.Constraints[36]
  sketch-geometry (17):
    g0: Circle CenterX=0 CenterY=0 CenterZ=0 NormalX=0 NormalY=0 NormalZ=1 AngleXU=0 Radius=50
    g1: LineSegment StartX=50 StartY=0 StartZ=0 EndX=49.99 EndY=0.99995 EndZ=0
    g2: LineSegment StartX=50 StartY=0 StartZ=0 EndX=49.4914 EndY=0.860982 EndZ=0
    g3: ArcOfCircle CenterX=2.57666 CenterY=0.525793 CenterZ=0 NormalX=0 NormalY=0 NormalZ=1 AngleXU=0 Radius=47.4157 StartAngle=0.0100002 EndAngle=3.1439
    g4: ArcOfCircle CenterX=-2.57666 CenterY=-0.525793 CenterZ=0 NormalX=0 NormalY=0 NormalZ=1 AngleXU=0 Radius=47.4157 StartAngle=3.15159 EndAngle=6.28549
    g5: LineSegment StartX=-50 StartY=0 StartZ=0 EndX=-49.99 EndY=-0.99995 EndZ=0
    g6: LineSegment StartX=-50 StartY=0 StartZ=0 EndX=-49.4914 EndY=-0.860982 EndZ=0
    g7: ArcOfCircle CenterX=-47.3389 CenterY=0.410606 CenterZ=0 NormalX=0 NormalY=0 NormalZ=1 AngleXU=0 Radius=2.5 StartAngle=3.67519 EndAngle=6.28549
    g8: ArcOfCircle CenterX=47.3389 CenterY=-0.410606 CenterZ=0 NormalX=0 NormalY=0 NormalZ=1 AngleXU=0 Radius=2.5 StartAngle=0.533599 EndAngle=3.1439
    g9: LineSegment StartX=-3.12999 StartY=-17.751 StartZ=0 EndX=13.8079 EndY=-11.5862 EndZ=0
    g10: LineSegment StartX=13.8079 StartY=-11.5862 StartZ=0 EndX=16.9378 EndY=6.16487 EndZ=0
    g11: LineSegment StartX=16.9378 StartY=6.16487 StartZ=0 EndX=3.12999 EndY=17.751 EndZ=0
    g12: LineSegment StartX=3.12999 StartY=17.751 StartZ=0 EndX=-13.8079 EndY=11.5862 EndZ=0
    g13: LineSegment StartX=-13.8079 StartY=11.5862 StartZ=0 EndX=-16.9378 EndY=-6.16487 EndZ=0
    g14: LineSegment StartX=-16.9378 StartY=-6.16487 StartZ=0 EndX=-3.12999 EndY=-17.751 EndZ=0
    g15: Circle CenterX=0 CenterY=0 CenterZ=0 NormalX=0 NormalY=0 NormalZ=1 AngleXU=0 Radius=18.0249
    g16: LineSegment StartX=0 StartY=0 StartZ=0 EndX=16.9378 EndY=6.16487 EndZ=0
  constraints (42):
    c: Diameter(g0) = 100
    c: PointOnObject(g1,g0)
    c: Coincident(g2,g1)
    c: PointOnObject(g1,g-1)
    c: Tangent(g3,g1) = -1.5708
    c: PointOnObject(g5,g-1)
    c: Coincident(g6,g5)
    c: Tangent(g7,g6) = -1.5708
    c: Tangent(g7,g3) = 1.5708
    c: Tangent(g8,g2) = -1.5708
    c: Tangent(g8,g4) = 1.5708
    c: PointOnObject(g5,g0)
    c: Coincident(g0,g-1)
    c: PointOnObject(g1,g0)
    c: Angle(g1,g2) = 0.523599
    c: Angle(g5,g6) = 0.523599
    c: Equal(g5,g1)
    c: PointOnObject(g4,g0)
    c: Equal(g7,g8)
    c: Equal(g3,g4)
    c: Equal(g5,g6)
    c: Distance(g1) = 1
    c: Radius(g8) = 2.5
    c: Coincident(g9,g10)
    c: Coincident(g10,g11)
    c: Coincident(g11,g12)
    c: Coincident(g12,g13)
    c: Coincident(g13,g14)
    c: Coincident(g14,g9)
    c: Equal(g9, g10-g14) x5
    c: PointOnObject(g9,g15)
    c: PointOnObject(g10,g15)
    c: PointOnObject(g11,g15)
    c: PointOnObject(g12,g15)
    c: PointOnObject(g13,g15)
    c: PointOnObject(g14,g15)
    c: Coincident(g15,g0)
    c: Distance(g9,g10) = 31.22
    c: Coincident(g16,g0)
    c: Coincident(g16,g10)
    c: Angle(g-1,g16) = 0.349066
    c: Tangent(g4,g5) = -1.5708
FEATURE [PartDesign::CoordinateSystem] LCS_cuchilla_salida002
  AttacherType = Attacher::AttachEngine3D
  MapMode = 11
  Placement = pos=(-3.6e-15,-9e-16,1.5) rot=(0,0,1;1.91986rad)
  Support = -> [Sketch023,Pad010]
FEATURE [Sketcher::SketchObject] Sketch025
  FullyConstrained = true
  MapMode = 5
  Placement = pos=(0,0,0) rot=(1,0,0;3.14159rad)
  Support = -> [Pad010]
  expr: Constraints[0] = Sketch023.Constraints[0]
  expr: Constraints[14] = Sketch023.Constraints[14]
  expr: Constraints[15] = Sketch023.Constraints[15]
  expr: Constraints[21] = Sketch023.Constraints[21]
  expr: Constraints[22] = Sketch023.Constraints[22]
  expr: Constraints[41] = Sketch023.Constraints[41]
  expr: Constraints[44] = Sketch023.Constraints[44]
  sketch-geometry (17):
    g0: Circle CenterX=0 CenterY=0 CenterZ=0 NormalX=0 NormalY=0 NormalZ=1 AngleXU=0 Radius=50
    g1: LineSegment StartX=50 StartY=0 StartZ=0 EndX=49.99 EndY=0.99995 EndZ=0
    g2: LineSegment StartX=50 StartY=0 StartZ=0 EndX=49.4914 EndY=0.860982 EndZ=0
    g3: ArcOfCircle CenterX=2.57666 CenterY=0.525793 CenterZ=0 NormalX=0 NormalY=0 NormalZ=1 AngleXU=0 Radius=47.4157 StartAngle=0.0100002 EndAngle=3.1439
    g4: ArcOfCircle CenterX=-2.57666 CenterY=-0.525793 CenterZ=0 NormalX=0 NormalY=0 NormalZ=1 AngleXU=0 Radius=47.4157 StartAngle=3.15159 EndAngle=6.28549
    g5: LineSegment StartX=-50 StartY=0 StartZ=0 EndX=-49.99 EndY=-0.99995 EndZ=0
    g6: LineSegment StartX=-50 StartY=0 StartZ=0 EndX=-49.4914 EndY=-0.860982 EndZ=0
    g7: ArcOfCircle CenterX=-47.3389 CenterY=0.410606 CenterZ=0 NormalX=0 NormalY=0 NormalZ=1 AngleXU=0 Radius=2.5 StartAngle=3.67519 EndAngle=6.28549
    g8: ArcOfCircle CenterX=47.3389 CenterY=-0.410606 CenterZ=0 NormalX=0 NormalY=0 NormalZ=1 AngleXU=0 Radius=2.5 StartAngle=0.533599 EndAngle=3.1439
    g9: LineSegment StartX=-3.12999 StartY=-17.751 StartZ=0 EndX=13.8079 EndY=-11.5862 EndZ=0
    g10: LineSegment StartX=13.8079 StartY=-11.5862 StartZ=0 EndX=16.9378 EndY=6.16487 EndZ=0
    g11: LineSegment StartX=16.9378 StartY=6.16487 StartZ=0 EndX=3.12999 EndY=17.751 EndZ=0
    g12: LineSegment StartX=3.12999 StartY=17.751 StartZ=0 EndX=-13.8079 EndY=11.5862 EndZ=0
    g13: LineSegment StartX=-13.8079 StartY=11.5862 StartZ=0 EndX=-16.9378 EndY=-6.16487 EndZ=0
    g14: LineSegment StartX=-16.9378 StartY=-6.16487 StartZ=0 EndX=-3.12999 EndY=-17.751 EndZ=0
    g15: Circle CenterX=0 CenterY=0 CenterZ=0 NormalX=0 NormalY=0 NormalZ=1 AngleXU=0 Radius=18.0249
    g16: LineSegment StartX=0 StartY=0 StartZ=0 EndX=16.9378 EndY=6.16487 EndZ=0
  constraints (42):
    c: Diameter(g0) = 100
    c: PointOnObject(g1,g0)
    c: Coincident(g2,g1)
    c: PointOnObject(g1,g-1)
    c: Tangent(g3,g1) = -1.5708
    c: PointOnObject(g5,g-1)
    c: Coincident(g6,g5)
    c: Tangent(g7,g6) = -1.5708
    c: Tangent(g7,g3) = 1.5708
    c: Tangent(g8,g2) = -1.5708
    c: Tangent(g8,g4) = 1.5708
    c: PointOnObject(g5,g0)
    c: Coincident(g0,g-1)
    c: PointOnObject(g1,g0)
    c: Angle(g1,g2) = 0.523599
    c: Angle(g5,g6) = 0.523599
    c: Equal(g5,g1)
    c: PointOnObject(g4,g0)
    c: Equal(g7,g8)
    c: Equal(g3,g4)
    c: Equal(g5,g6)
    c: Distance(g1) = 1
    c: Radius(g8) = 2.5
    c: Coincident(g9,g10)
    c: Coincident(g10,g11)
    c: Coincident(g11,g12)
    c: Coincident(g12,g13)
    c: Coincident(g13,g14)
    c: Coincident(g14,g9)
    c: Equal(g9, g10-g14) x5
    c: PointOnObject(g9,g15)
    c: PointOnObject(g10,g15)
    c: PointOnObject(g11,g15)
    c: PointOnObject(g12,g15)
    c: PointOnObject(g13,g15)
    c: PointOnObject(g14,g15)
    c: Coincident(g15,g0)
    c: Distance(g9,g10) = 31.22
    c: Coincident(g16,g0)
    c: Coincident(g16,g10)
    c: Angle(g-1,g16) = 0.349066
    c: Tangent(g4,g5) = -1.5708
FEATURE [PartDesign::CoordinateSystem] LCS_cuchilla_entrada002
  AttacherType = Attacher::AttachEngine3D
  MapMode = 11
  Placement = pos=(-3.6e-15,-9e-16,0) rot=(0,0,1;1.91986rad)
  Support = -> [Sketch025,Pad010]
FEATURE [PartDesign::Body] Body010  label="Cuchilla003"
  Group = -> [Sketch024,Pad010,LCS_cuchilla_entrada002,Sketch023,Sketch025,LCS_cuchilla_salida002]
  Origin = -> Origin010
  Tip = -> Pad010
FEATURE [Sketcher::SketchObject] Sketch027
  FullyConstrained = true
  MapMode = 5
  Support = -> [XY_Plane004]
  expr: Constraints[0] = dd.ddDiamteroExterno
  expr: Constraints[13] = dd.ddLargoPunta
  expr: Constraints[14] = dd.ddRadioMenor
  expr: Constraints[33] = dd.ddDistanceHexagono
  expr: Constraints[36] = dd.ddAngulo4
  expr: Constraints[8] = dd.ddAnguloPunta
  expr: Constraints[9] = dd.ddAnguloPunta
  sketch-geometry (17):
    g0: Circle CenterX=0 CenterY=0 CenterZ=0 NormalX=0 NormalY=0 NormalZ=1 AngleXU=0 Radius=50
    g1: LineSegment StartX=49.99 StartY=0 StartZ=0 EndX=49.99 EndY=1 EndZ=0
    g2: LineSegment StartX=49.99 StartY=0 StartZ=0 EndX=49.4126 EndY=1 EndZ=0
    g3: ArcOfCircle CenterX=2.61839 CenterY=1 CenterZ=0 NormalX=0 NormalY=0 NormalZ=1 AngleXU=0 Radius=47.3716 StartAngle=0 EndAngle=3.15663
    g4: ArcOfCircle CenterX=-2.61839 CenterY=-1 CenterZ=0 NormalX=0 NormalY=0 NormalZ=1 AngleXU=0 Radius=47.3716 StartAngle=3.14159 EndAngle=6.29822
    g5: LineSegment StartX=-49.99 StartY=0 StartZ=0 EndX=-49.99 EndY=-1 EndZ=0
    g6: LineSegment StartX=-49.99 StartY=0 StartZ=0 EndX=-49.4126 EndY=-1 EndZ=0
    g7: ArcOfCircle CenterX=-47.2476 CenterY=0.25 CenterZ=0 NormalX=0 NormalY=0 NormalZ=1 AngleXU=0 Radius=2.5 StartAngle=3.66519 EndAngle=6.29822
    g8: ArcOfCircle CenterX=47.2476 CenterY=-0.25 CenterZ=0 NormalX=0 NormalY=0 NormalZ=1 AngleXU=0 Radius=2.5 StartAngle=0.523599 EndAngle=3.15663
    g9: LineSegment StartX=-1.8e-15 StartY=-18.0249 StartZ=0 EndX=15.61 EndY=-9.01244 EndZ=0
    g10: LineSegment StartX=15.61 StartY=-9.01244 StartZ=0 EndX=15.61 EndY=9.01244 EndZ=0
    g11: LineSegment StartX=15.61 StartY=9.01244 StartZ=0 EndX=3.6e-15 EndY=18.0249 EndZ=0
    g12: LineSegment StartX=3.2e-15 StartY=18.0249 StartZ=0 EndX=-15.61 EndY=9.01244 EndZ=0
    g13: LineSegment StartX=-15.61 StartY=9.01244 StartZ=0 EndX=-15.61 EndY=-9.01244 EndZ=0
    g14: LineSegment StartX=-15.61 StartY=-9.01244 StartZ=0 EndX=-1.8e-15 EndY=-18.0249 EndZ=0
    g15: Circle CenterX=0 CenterY=0 CenterZ=0 NormalX=0 NormalY=0 NormalZ=1 AngleXU=0 Radius=18.0249
    g16: LineSegment StartX=0 StartY=0 StartZ=0 EndX=15.61 EndY=9.01244 EndZ=0
  constraints (42):
    c: Diameter(g0) = 100
    c: Tangent(g3,g1) = -1.5708
    c: Coincident(g6,g5)
    c: Tangent(g7,g6) = -1.5708
    c: Tangent(g7,g3) = 1.5708
    c: Tangent(g8,g2) = -1.5708
    c: Tangent(g8,g4) = 1.5708
    c: Coincident(g0,g-1)
    c: Angle(g1,g2) = 0.523599
    c: Angle(g5,g6) = 0.523599
    c: PointOnObject(g4,g0)
    c: Equal(g7,g8)
    c: Equal(g3,g4)
    c: Distance(g1) = 1
    c: Radius(g8) = 2.5
    c: Coincident(g9,g10)
    c: Coincident(g10,g11)
    c: Coincident(g11,g12)
    c: Coincident(g12,g13)
    c: Coincident(g13,g14)
    c: Coincident(g14,g9)
    c: Equal(g9, g10-g14) x5
    c: PointOnObject(g9,g15)
    c: PointOnObject(g10,g15)
    c: PointOnObject(g11,g15)
    c: PointOnObject(g12,g15)
    c: PointOnObject(g13,g15)
    c: PointOnObject(g14,g15)
    c: Coincident(g15,g0)
    c: Distance(g9,g10) = 31.22
    c: Coincident(g16,g0)
    c: Coincident(g16,g10)
    c: Angle(g-1,g16) = 0.523599
    c: Tangent(g4,g5) = -1.5708
    c: Vertical(g1)
    c: Coincident(g1,g2)
    c: PointOnObject(g1,g0)
    c: PointOnObject(g1,g-1)
    c: Horizontal(g2,g1)
    c: Vertical(g5)
    c: PointOnObject(g5,g-1)
    c: Horizontal(g6,g4)
FEATURE [PartDesign::Pad] Pad011
  Direction = (0,0,1)
  Length = 1.5
  Length2 = 10
  Profile = -> Sketch027
  Type = 0
  expr: Length = <<ddCuchillas>>.ddGrosorPlaca
FEATURE [Sketcher::SketchObject] Sketch026
  FullyConstrained = true
  MapMode = 5
  Placement = pos=(0,0,1.5) rot=(0,0,1;0rad)
  Support = -> [Pad011]
  expr: Constraints[0] = Sketch027.Constraints[0]
  expr: Constraints[14] = Sketch027.Constraints[8]
  expr: Constraints[15] = Sketch027.Constraints[9]
  expr: Constraints[21] = Sketch027.Constraints[13]
  expr: Constraints[22] = Sketch027.Constraints[14]
  expr: Constraints[41] = Sketch027.Constraints[33]
  expr: Constraints[44] = Sketch027.Constraints[36]
  sketch-geometry (17):
    g0: Circle CenterX=0 CenterY=0 CenterZ=0 NormalX=0 NormalY=0 NormalZ=1 AngleXU=0 Radius=50
    g1: LineSegment StartX=50 StartY=0 StartZ=0 EndX=49.99 EndY=0.99995 EndZ=0
    g2: LineSegment StartX=50 StartY=0 StartZ=0 EndX=49.4914 EndY=0.860982 EndZ=0
    g3: ArcOfCircle CenterX=2.57666 CenterY=0.525793 CenterZ=0 NormalX=0 NormalY=0 NormalZ=1 AngleXU=0 Radius=47.4157 StartAngle=0.0100002 EndAngle=3.1439
    g4: ArcOfCircle CenterX=-2.57666 CenterY=-0.525793 CenterZ=0 NormalX=0 NormalY=0 NormalZ=1 AngleXU=0 Radius=47.4157 StartAngle=3.15159 EndAngle=6.28549
    g5: LineSegment StartX=-50 StartY=0 StartZ=0 EndX=-49.99 EndY=-0.99995 EndZ=0
    g6: LineSegment StartX=-50 StartY=0 StartZ=0 EndX=-49.4914 EndY=-0.860982 EndZ=0
    g7: ArcOfCircle CenterX=-47.3389 CenterY=0.410606 CenterZ=0 NormalX=0 NormalY=0 NormalZ=1 AngleXU=0 Radius=2.5 StartAngle=3.67519 EndAngle=6.28549
    g8: ArcOfCircle CenterX=47.3389 CenterY=-0.410606 CenterZ=0 NormalX=0 NormalY=0 NormalZ=1 AngleXU=0 Radius=2.5 StartAngle=0.533599 EndAngle=3.1439
    g9: LineSegment StartX=-1.8e-15 StartY=-18.0249 StartZ=0 EndX=15.61 EndY=-9.01244 EndZ=0
    g10: LineSegment StartX=15.61 StartY=-9.01244 StartZ=0 EndX=15.61 EndY=9.01244 EndZ=0
    g11: LineSegment StartX=15.61 StartY=9.01244 StartZ=0 EndX=3.6e-15 EndY=18.0249 EndZ=0
    g12: LineSegment StartX=2.7e-15 StartY=18.0249 StartZ=0 EndX=-15.61 EndY=9.01244 EndZ=0
    g13: LineSegment StartX=-15.61 StartY=9.01244 StartZ=0 EndX=-15.61 EndY=-9.01244 EndZ=0
    g14: LineSegment StartX=-15.61 StartY=-9.01244 StartZ=0 EndX=-1.8e-15 EndY=-18.0249 EndZ=0
    g15: Circle CenterX=0 CenterY=0 CenterZ=0 NormalX=0 NormalY=0 NormalZ=1 AngleXU=0 Radius=18.0249
    g16: LineSegment StartX=0 StartY=0 StartZ=0 EndX=15.61 EndY=9.01244 EndZ=0
  constraints (42):
    c: Diameter(g0) = 100
    c: PointOnObject(g1,g0)
    c: Coincident(g2,g1)
    c: PointOnObject(g1,g-1)
    c: Tangent(g3,g1) = -1.5708
    c: PointOnObject(g5,g-1)
    c: Coincident(g6,g5)
    c: Tangent(g7,g6) = -1.5708
    c: Tangent(g7,g3) = 1.5708
    c: Tangent(g8,g2) = -1.5708
    c: Tangent(g8,g4) = 1.5708
    c: PointOnObject(g5,g0)
    c: Coincident(g0,g-1)
    c: PointOnObject(g1,g0)
    c: Angle(g1,g2) = 0.523599
    c: Angle(g5,g6) = 0.523599
    c: Equal(g5,g1)
    c: PointOnObject(g4,g0)
    c: Equal(g7,g8)
    c: Equal(g3,g4)
    c: Equal(g5,g6)
    c: Distance(g1) = 1
    c: Radius(g8) = 2.5
    c: Coincident(g9,g10)
    c: Coincident(g10,g11)
    c: Coincident(g11,g12)
    c: Coincident(g12,g13)
    c: Coincident(g13,g14)
    c: Coincident(g14,g9)
    c: Equal(g9, g10-g14) x5
    c: PointOnObject(g9,g15)
    c: PointOnObject(g10,g15)
    c: PointOnObject(g11,g15)
    c: PointOnObject(g12,g15)
    c: PointOnObject(g13,g15)
    c: PointOnObject(g14,g15)
    c: Coincident(g15,g0)
    c: Distance(g9,g10) = 31.22
    c: Coincident(g16,g0)
    c: Coincident(g16,g10)
    c: Angle(g-1,g16) = 0.523599
    c: Tangent(g4,g5) = -1.5708
FEATURE [PartDesign::CoordinateSystem] LCS_cuchilla_salida003
  AttacherType = Attacher::AttachEngine3D
  MapMode = 11
  Placement = pos=(-3.6e-15,-1.8e-15,1.5) rot=(0,0,1;2.0944rad)
  Support = -> [Sketch026,Pad011]
FEATURE [Sketcher::SketchObject] Sketch028
  FullyConstrained = true
  MapMode = 5
  Placement = pos=(0,0,0) rot=(1,0,0;3.14159rad)
  Support = -> [Pad011]
  expr: Constraints[0] = Sketch026.Constraints[0]
  expr: Constraints[14] = Sketch026.Constraints[14]
  expr: Constraints[15] = Sketch026.Constraints[15]
  expr: Constraints[21] = Sketch026.Constraints[21]
  expr: Constraints[22] = Sketch026.Constraints[22]
  expr: Constraints[41] = Sketch026.Constraints[41]
  expr: Constraints[44] = Sketch026.Constraints[44]
  sketch-geometry (17):
    g0: Circle CenterX=0 CenterY=0 CenterZ=0 NormalX=0 NormalY=0 NormalZ=1 AngleXU=0 Radius=50
    g1: LineSegment StartX=50 StartY=0 StartZ=0 EndX=49.99 EndY=0.99995 EndZ=0
    g2: LineSegment StartX=50 StartY=0 StartZ=0 EndX=49.4914 EndY=0.860982 EndZ=0
    g3: ArcOfCircle CenterX=2.57666 CenterY=0.525793 CenterZ=0 NormalX=0 NormalY=0 NormalZ=1 AngleXU=0 Radius=47.4157 StartAngle=0.0100002 EndAngle=3.1439
    g4: ArcOfCircle CenterX=-2.57666 CenterY=-0.525793 CenterZ=0 NormalX=0 NormalY=0 NormalZ=1 AngleXU=0 Radius=47.4157 StartAngle=3.15159 EndAngle=6.28549
    g5: LineSegment StartX=-50 StartY=0 StartZ=0 EndX=-49.99 EndY=-0.99995 EndZ=0
    g6: LineSegment StartX=-50 StartY=0 StartZ=0 EndX=-49.4914 EndY=-0.860982 EndZ=0
    g7: ArcOfCircle CenterX=-47.3389 CenterY=0.410606 CenterZ=0 NormalX=0 NormalY=0 NormalZ=1 AngleXU=0 Radius=2.5 StartAngle=3.67519 EndAngle=6.28549
    g8: ArcOfCircle CenterX=47.3389 CenterY=-0.410606 CenterZ=0 NormalX=0 NormalY=0 NormalZ=1 AngleXU=0 Radius=2.5 StartAngle=0.533599 EndAngle=3.1439
    g9: LineSegment StartX=0 StartY=-18.0249 StartZ=0 EndX=15.61 EndY=-9.01244 EndZ=0
    g10: LineSegment StartX=15.61 StartY=-9.01244 StartZ=0 EndX=15.61 EndY=9.01244 EndZ=0
    g11: LineSegment StartX=15.61 StartY=9.01244 StartZ=0 EndX=0 EndY=18.0249 EndZ=0
    g12: LineSegment StartX=3e-16 StartY=18.0249 StartZ=0 EndX=-15.61 EndY=9.01244 EndZ=0
    g13: LineSegment StartX=-15.61 StartY=9.01244 StartZ=0 EndX=-15.61 EndY=-9.01244 EndZ=0
    g14: LineSegment StartX=-15.61 StartY=-9.01244 StartZ=0 EndX=0 EndY=-18.0249 EndZ=0
    g15: Circle CenterX=0 CenterY=0 CenterZ=0 NormalX=0 NormalY=0 NormalZ=1 AngleXU=0 Radius=18.0249
    g16: LineSegment StartX=0 StartY=0 StartZ=0 EndX=15.61 EndY=9.01244 EndZ=0
  constraints (42):
    c: Diameter(g0) = 100
    c: PointOnObject(g1,g0)
    c: Coincident(g2,g1)
    c: PointOnObject(g1,g-1)
    c: Tangent(g3,g1) = -1.5708
    c: PointOnObject(g5,g-1)
    c: Coincident(g6,g5)
    c: Tangent(g7,g6) = -1.5708
    c: Tangent(g7,g3) = 1.5708
    c: Tangent(g8,g2) = -1.5708
    c: Tangent(g8,g4) = 1.5708
    c: PointOnObject(g5,g0)
    c: Coincident(g0,g-1)
    c: PointOnObject(g1,g0)
    c: Angle(g1,g2) = 0.523599
    c: Angle(g5,g6) = 0.523599
    c: Equal(g5,g1)
    c: PointOnObject(g4,g0)
    c: Equal(g7,g8)
    c: Equal(g3,g4)
    c: Equal(g5,g6)
    c: Distance(g1) = 1
    c: Radius(g8) = 2.5
    c: Coincident(g9,g10)
    c: Coincident(g10,g11)
    c: Coincident(g11,g12)
    c: Coincident(g12,g13)
    c: Coincident(g13,g14)
    c: Coincident(g14,g9)
    c: Equal(g9, g10-g14) x5
    c: PointOnObject(g9,g15)
    c: PointOnObject(g10,g15)
    c: PointOnObject(g11,g15)
    c: PointOnObject(g12,g15)
    c: PointOnObject(g13,g15)
    c: PointOnObject(g14,g15)
    c: Coincident(g15,g0)
    c: Distance(g9,g10) = 31.22
    c: Coincident(g16,g0)
    c: Coincident(g16,g10)
    c: Angle(g-1,g16) = 0.523599
    c: Tangent(g4,g5) = -1.5708
FEATURE [PartDesign::CoordinateSystem] LCS_cuchilla_entrada003
  AttacherType = Attacher::AttachEngine3D
  MapMode = 11
  Placement = pos=(-3.6e-15,-1.8e-15,0) rot=(0,0,1;2.0944rad)
  Support = -> [Sketch028,Pad011]
FEATURE [PartDesign::Body] Body011  label="Cuchilla004"
  Group = -> [Sketch027,Pad011,LCS_cuchilla_entrada003,Sketch026,Sketch028,LCS_cuchilla_salida003]
  Origin = -> Origin011
  Tip = -> Pad011
FEATURE [Sketcher::SketchObject] Sketch030
  FullyConstrained = true
  MapMode = 5
  Support = -> [XY_Plane005]
  expr: Constraints[0] = dd.ddDiamteroExterno
  expr: Constraints[13] = dd.ddLargoPunta
  expr: Constraints[14] = dd.ddRadioMenor
  expr: Constraints[33] = dd.ddDistanceHexagono
  expr: Constraints[36] = dd.ddAngulo5
  expr: Constraints[8] = dd.ddAnguloPunta
  expr: Constraints[9] = dd.ddAnguloPunta
  sketch-geometry (17):
    g0: Circle CenterX=0 CenterY=0 CenterZ=0 NormalX=0 NormalY=0 NormalZ=1 AngleXU=0 Radius=50
    g1: LineSegment StartX=49.99 StartY=0 StartZ=0 EndX=49.99 EndY=1 EndZ=0
    g2: LineSegment StartX=49.99 StartY=0 StartZ=0 EndX=49.4126 EndY=1 EndZ=0
    g3: ArcOfCircle CenterX=2.61839 CenterY=1 CenterZ=0 NormalX=0 NormalY=0 NormalZ=1 AngleXU=0 Radius=47.3716 StartAngle=0 EndAngle=3.15663
    g4: ArcOfCircle CenterX=-2.61839 CenterY=-1 CenterZ=0 NormalX=0 NormalY=0 NormalZ=1 AngleXU=0 Radius=47.3716 StartAngle=3.14159 EndAngle=6.29822
    g5: LineSegment StartX=-49.99 StartY=0 StartZ=0 EndX=-49.99 EndY=-1 EndZ=0
    g6: LineSegment StartX=-49.99 StartY=0 StartZ=0 EndX=-49.4126 EndY=-1 EndZ=0
    g7: ArcOfCircle CenterX=-47.2476 CenterY=0.25 CenterZ=0 NormalX=0 NormalY=0 NormalZ=1 AngleXU=0 Radius=2.5 StartAngle=3.66519 EndAngle=6.29822
    g8: ArcOfCircle CenterX=47.2476 CenterY=-0.25 CenterZ=0 NormalX=0 NormalY=0 NormalZ=1 AngleXU=0 Radius=2.5 StartAngle=0.523599 EndAngle=3.15663
    g9: LineSegment StartX=3.12999 StartY=-17.751 StartZ=0 EndX=16.9378 EndY=-6.16487 EndZ=0
    g10: LineSegment StartX=16.9378 StartY=-6.16487 StartZ=0 EndX=13.8079 EndY=11.5862 EndZ=0
    g11: LineSegment StartX=13.8079 StartY=11.5862 StartZ=0 EndX=-3.12999 EndY=17.751 EndZ=0
    g12: LineSegment StartX=-3.12999 StartY=17.751 StartZ=0 EndX=-16.9378 EndY=6.16487 EndZ=0
    g13: LineSegment StartX=-16.9378 StartY=6.16487 StartZ=0 EndX=-13.8079 EndY=-11.5862 EndZ=0
    g14: LineSegment StartX=-13.8079 StartY=-11.5862 StartZ=0 EndX=3.12999 EndY=-17.751 EndZ=0
    g15: Circle CenterX=0 CenterY=0 CenterZ=0 NormalX=0 NormalY=0 NormalZ=1 AngleXU=0 Radius=18.0249
    g16: LineSegment StartX=0 StartY=0 StartZ=0 EndX=13.8079 EndY=11.5862 EndZ=0
  constraints (42):
    c: Diameter(g0) = 100
    c: Tangent(g3,g1) = -1.5708
    c: Coincident(g6,g5)
    c: Tangent(g7,g6) = -1.5708
    c: Tangent(g7,g3) = 1.5708
    c: Tangent(g8,g2) = -1.5708
    c: Tangent(g8,g4) = 1.5708
    c: Coincident(g0,g-1)
    c: Angle(g1,g2) = 0.523599
    c: Angle(g5,g6) = 0.523599
    c: PointOnObject(g4,g0)
    c: Equal(g7,g8)
    c: Equal(g3,g4)
    c: Distance(g1) = 1
    c: Radius(g8) = 2.5
    c: Coincident(g9,g10)
    c: Coincident(g10,g11)
    c: Coincident(g11,g12)
    c: Coincident(g12,g13)
    c: Coincident(g13,g14)
    c: Coincident(g14,g9)
    c: Equal(g9, g10-g14) x5
    c: PointOnObject(g9,g15)
    c: PointOnObject(g10,g15)
    c: PointOnObject(g11,g15)
    c: PointOnObject(g12,g15)
    c: PointOnObject(g13,g15)
    c: PointOnObject(g14,g15)
    c: Coincident(g15,g0)
    c: Distance(g9,g10) = 31.22
    c: Coincident(g16,g0)
    c: Coincident(g16,g10)
    c: Angle(g-1,g16) = 0.698132
    c: Tangent(g4,g5) = -1.5708
    c: Vertical(g1)
    c: Coincident(g1,g2)
    c: PointOnObject(g1,g0)
    c: PointOnObject(g1,g-1)
    c: Horizontal(g2,g1)
    c: Vertical(g5)
    c: PointOnObject(g5,g-1)
    c: Horizontal(g6,g4)
FEATURE [PartDesign::Pad] Pad012
  Direction = (0,0,1)
  Length = 1.5
  Length2 = 10
  Profile = -> Sketch030
  Type = 0
  expr: Length = <<ddCuchillas>>.ddGrosorPlaca
FEATURE [Sketcher::SketchObject] Sketch029
  FullyConstrained = true
  MapMode = 5
  Placement = pos=(0,0,1.5) rot=(0,0,1;0rad)
  Support = -> [Pad012]
  expr: Constraints[0] = Sketch030.Constraints[0]
  expr: Constraints[14] = Sketch030.Constraints[8]
  expr: Constraints[15] = Sketch030.Constraints[9]
  expr: Constraints[21] = Sketch030.Constraints[13]
  expr: Constraints[22] = Sketch030.Constraints[14]
  expr: Constraints[41] = Sketch030.Constraints[33]
  expr: Constraints[44] = Sketch030.Constraints[36]
  sketch-geometry (17):
    g0: Circle CenterX=0 CenterY=0 CenterZ=0 NormalX=0 NormalY=0 NormalZ=1 AngleXU=0 Radius=50
    g1: LineSegment StartX=50 StartY=0 StartZ=0 EndX=49.99 EndY=0.99995 EndZ=0
    g2: LineSegment StartX=50 StartY=0 StartZ=0 EndX=49.4914 EndY=0.860982 EndZ=0
    g3: ArcOfCircle CenterX=2.57666 CenterY=0.525793 CenterZ=0 NormalX=0 NormalY=0 NormalZ=1 AngleXU=0 Radius=47.4157 StartAngle=0.0100002 EndAngle=3.1439
    g4: ArcOfCircle CenterX=-2.57666 CenterY=-0.525793 CenterZ=0 NormalX=0 NormalY=0 NormalZ=1 AngleXU=0 Radius=47.4157 StartAngle=3.15159 EndAngle=6.28549
    g5: LineSegment StartX=-50 StartY=0 StartZ=0 EndX=-49.99 EndY=-0.99995 EndZ=0
    g6: LineSegment StartX=-50 StartY=0 StartZ=0 EndX=-49.4914 EndY=-0.860982 EndZ=0
    g7: ArcOfCircle CenterX=-47.3389 CenterY=0.410606 CenterZ=0 NormalX=0 NormalY=0 NormalZ=1 AngleXU=0 Radius=2.5 StartAngle=3.67519 EndAngle=6.28549
    g8: ArcOfCircle CenterX=47.3389 CenterY=-0.410606 CenterZ=0 NormalX=0 NormalY=0 NormalZ=1 AngleXU=0 Radius=2.5 StartAngle=0.533599 EndAngle=3.1439
    g9: LineSegment StartX=3.12999 StartY=-17.751 StartZ=0 EndX=16.9378 EndY=-6.16487 EndZ=0
    g10: LineSegment StartX=16.9378 StartY=-6.16487 StartZ=0 EndX=13.8079 EndY=11.5862 EndZ=0
    g11: LineSegment StartX=13.8079 StartY=11.5862 StartZ=0 EndX=-3.12999 EndY=17.751 EndZ=0
    g12: LineSegment StartX=-3.12999 StartY=17.751 StartZ=0 EndX=-16.9378 EndY=6.16487 EndZ=0
    g13: LineSegment StartX=-16.9378 StartY=6.16487 StartZ=0 EndX=-13.8079 EndY=-11.5862 EndZ=0
    g14: LineSegment StartX=-13.8079 StartY=-11.5862 StartZ=0 EndX=3.12999 EndY=-17.751 EndZ=0
    g15: Circle CenterX=0 CenterY=0 CenterZ=0 NormalX=0 NormalY=0 NormalZ=1 AngleXU=0 Radius=18.0249
    g16: LineSegment StartX=0 StartY=0 StartZ=0 EndX=13.8079 EndY=11.5862 EndZ=0
  constraints (42):
    c: Diameter(g0) = 100
    c: PointOnObject(g1,g0)
    c: Coincident(g2,g1)
    c: PointOnObject(g1,g-1)
    c: Tangent(g3,g1) = -1.5708
    c: PointOnObject(g5,g-1)
    c: Coincident(g6,g5)
    c: Tangent(g7,g6) = -1.5708
    c: Tangent(g7,g3) = 1.5708
    c: Tangent(g8,g2) = -1.5708
    c: Tangent(g8,g4) = 1.5708
    c: PointOnObject(g5,g0)
    c: Coincident(g0,g-1)
    c: PointOnObject(g1,g0)
    c: Angle(g1,g2) = 0.523599
    c: Angle(g5,g6) = 0.523599
    c: Equal(g5,g1)
    c: PointOnObject(g4,g0)
    c: Equal(g7,g8)
    c: Equal(g3,g4)
    c: Equal(g5,g6)
    c: Distance(g1) = 1
    c: Radius(g8) = 2.5
    c: Coincident(g9,g10)
    c: Coincident(g10,g11)
    c: Coincident(g11,g12)
    c: Coincident(g12,g13)
    c: Coincident(g13,g14)
    c: Coincident(g14,g9)
    c: Equal(g9, g10-g14) x5
    c: PointOnObject(g9,g15)
    c: PointOnObject(g10,g15)
    c: PointOnObject(g11,g15)
    c: PointOnObject(g12,g15)
    c: PointOnObject(g13,g15)
    c: PointOnObject(g14,g15)
    c: Coincident(g15,g0)
    c: Distance(g9,g10) = 31.22
    c: Coincident(g16,g0)
    c: Coincident(g16,g10)
    c: Angle(g-1,g16) = 0.698132
    c: Tangent(g4,g5) = -1.5708
FEATURE [PartDesign::CoordinateSystem] LCS_cuchilla_salida004
  AttacherType = Attacher::AttachEngine3D
  MapMode = 11
  Placement = pos=(0,0,1.5) rot=(0,0,1;2.26893rad)
  Support = -> [Sketch029,Pad012]
FEATURE [Sketcher::SketchObject] Sketch031
  FullyConstrained = true
  MapMode = 5
  Placement = pos=(0,0,0) rot=(1,0,0;3.14159rad)
  Support = -> [Pad012]
  expr: Constraints[0] = Sketch029.Constraints[0]
  expr: Constraints[14] = Sketch029.Constraints[14]
  expr: Constraints[15] = Sketch029.Constraints[15]
  expr: Constraints[21] = Sketch029.Constraints[21]
  expr: Constraints[22] = Sketch029.Constraints[22]
  expr: Constraints[41] = Sketch029.Constraints[41]
  expr: Constraints[44] = Sketch029.Constraints[44]
  sketch-geometry (17):
    g0: Circle CenterX=0 CenterY=0 CenterZ=0 NormalX=0 NormalY=0 NormalZ=1 AngleXU=0 Radius=50
    g1: LineSegment StartX=50 StartY=0 StartZ=0 EndX=49.99 EndY=0.99995 EndZ=0
    g2: LineSegment StartX=50 StartY=0 StartZ=0 EndX=49.4914 EndY=0.860982 EndZ=0
    g3: ArcOfCircle CenterX=2.57666 CenterY=0.525793 CenterZ=0 NormalX=0 NormalY=0 NormalZ=1 AngleXU=0 Radius=47.4157 StartAngle=0.0100002 EndAngle=3.1439
    g4: ArcOfCircle CenterX=-2.57666 CenterY=-0.525793 CenterZ=0 NormalX=0 NormalY=0 NormalZ=1 AngleXU=0 Radius=47.4157 StartAngle=3.15159 EndAngle=6.28549
    g5: LineSegment StartX=-50 StartY=0 StartZ=0 EndX=-49.99 EndY=-0.99995 EndZ=0
    g6: LineSegment StartX=-50 StartY=0 StartZ=0 EndX=-49.4914 EndY=-0.860982 EndZ=0
    g7: ArcOfCircle CenterX=-47.3389 CenterY=0.410606 CenterZ=0 NormalX=0 NormalY=0 NormalZ=1 AngleXU=0 Radius=2.5 StartAngle=3.67519 EndAngle=6.28549
    g8: ArcOfCircle CenterX=47.3389 CenterY=-0.410606 CenterZ=0 NormalX=0 NormalY=0 NormalZ=1 AngleXU=0 Radius=2.5 StartAngle=0.533599 EndAngle=3.1439
    g9: LineSegment StartX=3.12999 StartY=-17.751 StartZ=0 EndX=16.9378 EndY=-6.16487 EndZ=0
    g10: LineSegment StartX=16.9378 StartY=-6.16487 StartZ=0 EndX=13.8079 EndY=11.5862 EndZ=0
    g11: LineSegment StartX=13.8079 StartY=11.5862 StartZ=0 EndX=-3.12999 EndY=17.751 EndZ=0
    g12: LineSegment StartX=-3.12999 StartY=17.751 StartZ=0 EndX=-16.9378 EndY=6.16487 EndZ=0
    g13: LineSegment StartX=-16.9378 StartY=6.16487 StartZ=0 EndX=-13.8079 EndY=-11.5862 EndZ=0
    g14: LineSegment StartX=-13.8079 StartY=-11.5862 StartZ=0 EndX=3.12999 EndY=-17.751 EndZ=0
    g15: Circle CenterX=0 CenterY=0 CenterZ=0 NormalX=0 NormalY=0 NormalZ=1 AngleXU=0 Radius=18.0249
    g16: LineSegment StartX=0 StartY=0 StartZ=0 EndX=13.8079 EndY=11.5862 EndZ=0
  constraints (42):
    c: Diameter(g0) = 100
    c: PointOnObject(g1,g0)
    c: Coincident(g2,g1)
    c: PointOnObject(g1,g-1)
    c: Tangent(g3,g1) = -1.5708
    c: PointOnObject(g5,g-1)
    c: Coincident(g6,g5)
    c: Tangent(g7,g6) = -1.5708
    c: Tangent(g7,g3) = 1.5708
    c: Tangent(g8,g2) = -1.5708
    c: Tangent(g8,g4) = 1.5708
    c: PointOnObject(g5,g0)
    c: Coincident(g0,g-1)
    c: PointOnObject(g1,g0)
    c: Angle(g1,g2) = 0.523599
    c: Angle(g5,g6) = 0.523599
    c: Equal(g5,g1)
    c: PointOnObject(g4,g0)
    c: Equal(g7,g8)
    c: Equal(g3,g4)
    c: Equal(g5,g6)
    c: Distance(g1) = 1
    c: Radius(g8) = 2.5
    c: Coincident(g9,g10)
    c: Coincident(g10,g11)
    c: Coincident(g11,g12)
    c: Coincident(g12,g13)
    c: Coincident(g13,g14)
    c: Coincident(g14,g9)
    c: Equal(g9, g10-g14) x5
    c: PointOnObject(g9,g15)
    c: PointOnObject(g10,g15)
    c: PointOnObject(g11,g15)
    c: PointOnObject(g12,g15)
    c: PointOnObject(g13,g15)
    c: PointOnObject(g14,g15)
    c: Coincident(g15,g0)
    c: Distance(g9,g10) = 31.22
    c: Coincident(g16,g0)
    c: Coincident(g16,g10)
    c: Angle(g-1,g16) = 0.698132
    c: Tangent(g4,g5) = -1.5708
FEATURE [PartDesign::CoordinateSystem] LCS_cuchilla_entrada004
  AttacherType = Attacher::AttachEngine3D
  MapMode = 11
  Placement = pos=(0,0,0) rot=(0,0,1;2.26893rad)
  Support = -> [Sketch031,Pad012]
FEATURE [PartDesign::Body] Body012  label="Cuchilla005"
  Group = -> [Sketch030,Pad012,LCS_cuchilla_entrada004,Sketch029,Sketch031,LCS_cuchilla_salida004]
  Origin = -> Origin012
  Tip = -> Pad012
FEATURE [Sketcher::SketchObject] Sketch033
  FullyConstrained = true
  MapMode = 5
  Support = -> [XY_Plane006]
  expr: Constraints[0] = dd.ddDiamteroExterno
  expr: Constraints[13] = dd.ddLargoPunta
  expr: Constraints[14] = dd.ddRadioMenor
  expr: Constraints[33] = dd.ddDistanceHexagono
  expr: Constraints[36] = dd.ddAngulo6
  expr: Constraints[8] = dd.ddAnguloPunta
  expr: Constraints[9] = dd.ddAnguloPunta
  sketch-geometry (17):
    g0: Circle CenterX=0 CenterY=0 CenterZ=0 NormalX=0 NormalY=0 NormalZ=1 AngleXU=0 Radius=50
    g1: LineSegment StartX=49.99 StartY=0 StartZ=0 EndX=49.99 EndY=1 EndZ=0
    g2: LineSegment StartX=49.99 StartY=0 StartZ=0 EndX=49.4126 EndY=1 EndZ=0
    g3: ArcOfCircle CenterX=2.61839 CenterY=1 CenterZ=0 NormalX=0 NormalY=0 NormalZ=1 AngleXU=0 Radius=47.3716 StartAngle=0 EndAngle=3.15663
    g4: ArcOfCircle CenterX=-2.61839 CenterY=-1 CenterZ=0 NormalX=0 NormalY=0 NormalZ=1 AngleXU=0 Radius=47.3716 StartAngle=3.14159 EndAngle=6.29822
    g5: LineSegment StartX=-49.99 StartY=0 StartZ=0 EndX=-49.99 EndY=-1 EndZ=0
    g6: LineSegment StartX=-49.99 StartY=0 StartZ=0 EndX=-49.4126 EndY=-1 EndZ=0
    g7: ArcOfCircle CenterX=-47.2476 CenterY=0.25 CenterZ=0 NormalX=0 NormalY=0 NormalZ=1 AngleXU=0 Radius=2.5 StartAngle=3.66519 EndAngle=6.29822
    g8: ArcOfCircle CenterX=47.2476 CenterY=-0.25 CenterZ=0 NormalX=0 NormalY=0 NormalZ=1 AngleXU=0 Radius=2.5 StartAngle=0.523599 EndAngle=3.15663
    g9: LineSegment StartX=6.16487 StartY=-16.9378 StartZ=0 EndX=17.751 EndY=-3.12999 EndZ=0
    g10: LineSegment StartX=17.751 StartY=-3.12999 StartZ=0 EndX=11.5862 EndY=13.8079 EndZ=0
    g11: LineSegment StartX=11.5862 StartY=13.8079 StartZ=0 EndX=-6.16487 EndY=16.9378 EndZ=0
    g12: LineSegment StartX=-6.16487 StartY=16.9378 StartZ=0 EndX=-17.751 EndY=3.12999 EndZ=0
    g13: LineSegment StartX=-17.751 StartY=3.12999 StartZ=0 EndX=-11.5862 EndY=-13.8079 EndZ=0
    g14: LineSegment StartX=-11.5862 StartY=-13.8079 StartZ=0 EndX=6.16487 EndY=-16.9378 EndZ=0
    g15: Circle CenterX=0 CenterY=0 CenterZ=0 NormalX=0 NormalY=0 NormalZ=1 AngleXU=0 Radius=18.0249
    g16: LineSegment StartX=0 StartY=0 StartZ=0 EndX=11.5862 EndY=13.8079 EndZ=0
  constraints (42):
    c: Diameter(g0) = 100
    c: Tangent(g3,g1) = -1.5708
    c: Coincident(g6,g5)
    c: Tangent(g7,g6) = -1.5708
    c: Tangent(g7,g3) = 1.5708
    c: Tangent(g8,g2) = -1.5708
    c: Tangent(g8,g4) = 1.5708
    c: Coincident(g0,g-1)
    c: Angle(g1,g2) = 0.523599
    c: Angle(g5,g6) = 0.523599
    c: PointOnObject(g4,g0)
    c: Equal(g7,g8)
    c: Equal(g3,g4)
    c: Distance(g1) = 1
    c: Radius(g8) = 2.5
    c: Coincident(g9,g10)
    c: Coincident(g10,g11)
    c: Coincident(g11,g12)
    c: Coincident(g12,g13)
    c: Coincident(g13,g14)
    c: Coincident(g14,g9)
    c: Equal(g9, g10-g14) x5
    c: PointOnObject(g9,g15)
    c: PointOnObject(g10,g15)
    c: PointOnObject(g11,g15)
    c: PointOnObject(g12,g15)
    c: PointOnObject(g13,g15)
    c: PointOnObject(g14,g15)
    c: Coincident(g15,g0)
    c: Distance(g9,g10) = 31.22
    c: Coincident(g16,g0)
    c: Coincident(g16,g10)
    c: Angle(g-1,g16) = 0.872665
    c: Tangent(g4,g5) = -1.5708
    c: Vertical(g1)
    c: Coincident(g1,g2)
    c: PointOnObject(g1,g0)
    c: PointOnObject(g1,g-1)
    c: Horizontal(g2,g1)
    c: Vertical(g5)
    c: PointOnObject(g5,g-1)
    c: Horizontal(g6,g4)
FEATURE [PartDesign::Pad] Pad013
  Direction = (0,0,1)
  Length = 1.5
  Length2 = 10
  Profile = -> Sketch033
  Type = 0
  expr: Length = <<ddCuchillas>>.ddGrosorPlaca
FEATURE [Sketcher::SketchObject] Sketch032
  FullyConstrained = true
  MapMode = 5
  Placement = pos=(0,0,1.5) rot=(0,0,1;0rad)
  Support = -> [Pad013]
  expr: Constraints[0] = Sketch033.Constraints[0]
  expr: Constraints[14] = Sketch033.Constraints[8]
  expr: Constraints[15] = Sketch033.Constraints[9]
  expr: Constraints[21] = Sketch033.Constraints[13]
  expr: Constraints[22] = Sketch033.Constraints[14]
  expr: Constraints[41] = Sketch033.Constraints[33]
  expr: Constraints[44] = Sketch033.Constraints[36]
  sketch-geometry (17):
    g0: Circle CenterX=0 CenterY=0 CenterZ=0 NormalX=0 NormalY=0 NormalZ=1 AngleXU=0 Radius=50
    g1: LineSegment StartX=50 StartY=0 StartZ=0 EndX=49.99 EndY=0.99995 EndZ=0
    g2: LineSegment StartX=50 StartY=0 StartZ=0 EndX=49.4914 EndY=0.860982 EndZ=0
    g3: ArcOfCircle CenterX=2.57666 CenterY=0.525793 CenterZ=0 NormalX=0 NormalY=0 NormalZ=1 AngleXU=0 Radius=47.4157 StartAngle=0.0100002 EndAngle=3.1439
    g4: ArcOfCircle CenterX=-2.57666 CenterY=-0.525793 CenterZ=0 NormalX=0 NormalY=0 NormalZ=1 AngleXU=0 Radius=47.4157 StartAngle=3.15159 EndAngle=6.28549
    g5: LineSegment StartX=-50 StartY=0 StartZ=0 EndX=-49.99 EndY=-0.99995 EndZ=0
    g6: LineSegment StartX=-50 StartY=0 StartZ=0 EndX=-49.4914 EndY=-0.860982 EndZ=0
    g7: ArcOfCircle CenterX=-47.3389 CenterY=0.410606 CenterZ=0 NormalX=0 NormalY=0 NormalZ=1 AngleXU=0 Radius=2.5 StartAngle=3.67519 EndAngle=6.28549
    g8: ArcOfCircle CenterX=47.3389 CenterY=-0.410606 CenterZ=0 NormalX=0 NormalY=0 NormalZ=1 AngleXU=0 Radius=2.5 StartAngle=0.533599 EndAngle=3.1439
    g9: LineSegment StartX=6.16487 StartY=-16.9378 StartZ=0 EndX=17.751 EndY=-3.12999 EndZ=0
    g10: LineSegment StartX=17.751 StartY=-3.12999 StartZ=0 EndX=11.5862 EndY=13.8079 EndZ=0
    g11: LineSegment StartX=11.5862 StartY=13.8079 StartZ=0 EndX=-6.16487 EndY=16.9378 EndZ=0
    g12: LineSegment StartX=-6.16487 StartY=16.9378 StartZ=0 EndX=-17.751 EndY=3.12999 EndZ=0
    g13: LineSegment StartX=-17.751 StartY=3.12999 StartZ=0 EndX=-11.5862 EndY=-13.8079 EndZ=0
    g14: LineSegment StartX=-11.5862 StartY=-13.8079 StartZ=0 EndX=6.16487 EndY=-16.9378 EndZ=0
    g15: Circle CenterX=0 CenterY=0 CenterZ=0 NormalX=0 NormalY=0 NormalZ=1 AngleXU=0 Radius=18.0249
    g16: LineSegment StartX=0 StartY=0 StartZ=0 EndX=11.5862 EndY=13.8079 EndZ=0
  constraints (42):
    c: Diameter(g0) = 100
    c: PointOnObject(g1,g0)
    c: Coincident(g2,g1)
    c: PointOnObject(g1,g-1)
    c: Tangent(g3,g1) = -1.5708
    c: PointOnObject(g5,g-1)
    c: Coincident(g6,g5)
    c: Tangent(g7,g6) = -1.5708
    c: Tangent(g7,g3) = 1.5708
    c: Tangent(g8,g2) = -1.5708
    c: Tangent(g8,g4) = 1.5708
    c: PointOnObject(g5,g0)
    c: Coincident(g0,g-1)
    c: PointOnObject(g1,g0)
    c: Angle(g1,g2) = 0.523599
    c: Angle(g5,g6) = 0.523599
    c: Equal(g5,g1)
    c: PointOnObject(g4,g0)
    c: Equal(g7,g8)
    c: Equal(g3,g4)
    c: Equal(g5,g6)
    c: Distance(g1) = 1
    c: Radius(g8) = 2.5
    c: Coincident(g9,g10)
    c: Coincident(g10,g11)
    c: Coincident(g11,g12)
    c: Coincident(g12,g13)
    c: Coincident(g13,g14)
    c: Coincident(g14,g9)
    c: Equal(g9, g10-g14) x5
    c: PointOnObject(g9,g15)
    c: PointOnObject(g10,g15)
    c: PointOnObject(g11,g15)
    c: PointOnObject(g12,g15)
    c: PointOnObject(g13,g15)
    c: PointOnObject(g14,g15)
    c: Coincident(g15,g0)
    c: Distance(g9,g10) = 31.22
    c: Coincident(g16,g0)
    c: Coincident(g16,g10)
    c: Angle(g-1,g16) = 0.872665
    c: Tangent(g4,g5) = -1.5708
FEATURE [PartDesign::CoordinateSystem] LCS_cuchilla_salida005
  AttacherType = Attacher::AttachEngine3D
  MapMode = 11
  Placement = pos=(-1.8e-15,-1.8e-15,1.5) rot=(0,0,1;2.44346rad)
  Support = -> [Sketch032,Pad013]
FEATURE [Sketcher::SketchObject] Sketch034
  FullyConstrained = true
  MapMode = 5
  Placement = pos=(0,0,0) rot=(1,0,0;3.14159rad)
  Support = -> [Pad013]
  expr: Constraints[0] = Sketch032.Constraints[0]
  expr: Constraints[14] = Sketch032.Constraints[14]
  expr: Constraints[15] = Sketch032.Constraints[15]
  expr: Constraints[21] = Sketch032.Constraints[21]
  expr: Constraints[22] = Sketch032.Constraints[22]
  expr: Constraints[41] = Sketch032.Constraints[41]
  expr: Constraints[44] = Sketch032.Constraints[44]
  sketch-geometry (17):
    g0: Circle CenterX=0 CenterY=0 CenterZ=0 NormalX=0 NormalY=0 NormalZ=1 AngleXU=0 Radius=50
    g1: LineSegment StartX=50 StartY=0 StartZ=0 EndX=49.99 EndY=0.99995 EndZ=0
    g2: LineSegment StartX=50 StartY=0 StartZ=0 EndX=49.4914 EndY=0.860982 EndZ=0
    g3: ArcOfCircle CenterX=2.57666 CenterY=0.525793 CenterZ=0 NormalX=0 NormalY=0 NormalZ=1 AngleXU=0 Radius=47.4157 StartAngle=0.0100002 EndAngle=3.1439
    g4: ArcOfCircle CenterX=-2.57666 CenterY=-0.525793 CenterZ=0 NormalX=0 NormalY=0 NormalZ=1 AngleXU=0 Radius=47.4157 StartAngle=3.15159 EndAngle=6.28549
    g5: LineSegment StartX=-50 StartY=0 StartZ=0 EndX=-49.99 EndY=-0.99995 EndZ=0
    g6: LineSegment StartX=-50 StartY=0 StartZ=0 EndX=-49.4914 EndY=-0.860982 EndZ=0
    g7: ArcOfCircle CenterX=-47.3389 CenterY=0.410606 CenterZ=0 NormalX=0 NormalY=0 NormalZ=1 AngleXU=0 Radius=2.5 StartAngle=3.67519 EndAngle=6.28549
    g8: ArcOfCircle CenterX=47.3389 CenterY=-0.410606 CenterZ=0 NormalX=0 NormalY=0 NormalZ=1 AngleXU=0 Radius=2.5 StartAngle=0.533599 EndAngle=3.1439
    g9: LineSegment StartX=6.16487 StartY=-16.9378 StartZ=0 EndX=17.751 EndY=-3.12999 EndZ=0
    g10: LineSegment StartX=17.751 StartY=-3.12999 StartZ=0 EndX=11.5862 EndY=13.8079 EndZ=0
    g11: LineSegment StartX=11.5862 StartY=13.8079 StartZ=0 EndX=-6.16487 EndY=16.9378 EndZ=0
    g12: LineSegment StartX=-6.16487 StartY=16.9378 StartZ=0 EndX=-17.751 EndY=3.12999 EndZ=0
    g13: LineSegment StartX=-17.751 StartY=3.12999 StartZ=0 EndX=-11.5862 EndY=-13.8079 EndZ=0
    g14: LineSegment StartX=-11.5862 StartY=-13.8079 StartZ=0 EndX=6.16487 EndY=-16.9378 EndZ=0
    g15: Circle CenterX=0 CenterY=0 CenterZ=0 NormalX=0 NormalY=0 NormalZ=1 AngleXU=0 Radius=18.0249
    g16: LineSegment StartX=0 StartY=0 StartZ=0 EndX=11.5862 EndY=13.8079 EndZ=0
  constraints (42):
    c: Diameter(g0) = 100
    c: PointOnObject(g1,g0)
    c: Coincident(g2,g1)
    c: PointOnObject(g1,g-1)
    c: Tangent(g3,g1) = -1.5708
    c: PointOnObject(g5,g-1)
    c: Coincident(g6,g5)
    c: Tangent(g7,g6) = -1.5708
    c: Tangent(g7,g3) = 1.5708
    c: Tangent(g8,g2) = -1.5708
    c: Tangent(g8,g4) = 1.5708
    c: PointOnObject(g5,g0)
    c: Coincident(g0,g-1)
    c: PointOnObject(g1,g0)
    c: Angle(g1,g2) = 0.523599
    c: Angle(g5,g6) = 0.523599
    c: Equal(g5,g1)
    c: PointOnObject(g4,g0)
    c: Equal(g7,g8)
    c: Equal(g3,g4)
    c: Equal(g5,g6)
    c: Distance(g1) = 1
    c: Radius(g8) = 2.5
    c: Coincident(g9,g10)
    c: Coincident(g10,g11)
    c: Coincident(g11,g12)
    c: Coincident(g12,g13)
    c: Coincident(g13,g14)
    c: Coincident(g14,g9)
    c: Equal(g9, g10-g14) x5
    c: PointOnObject(g9,g15)
    c: PointOnObject(g10,g15)
    c: PointOnObject(g11,g15)
    c: PointOnObject(g12,g15)
    c: PointOnObject(g13,g15)
    c: PointOnObject(g14,g15)
    c: Coincident(g15,g0)
    c: Distance(g9,g10) = 31.22
    c: Coincident(g16,g0)
    c: Coincident(g16,g10)
    c: Angle(g-1,g16) = 0.872665
    c: Tangent(g4,g5) = -1.5708
FEATURE [PartDesign::CoordinateSystem] LCS_cuchilla_entrada005
  AttacherType = Attacher::AttachEngine3D
  MapMode = 11
  Placement = pos=(-1.8e-15,-1.8e-15,0) rot=(0,0,1;2.44346rad)
  Support = -> [Sketch034,Pad013]
FEATURE [PartDesign::Body] Body013  label="Cuchilla006"
  Group = -> [Sketch033,Pad013,LCS_cuchilla_entrada005,Sketch032,Sketch034,LCS_cuchilla_salida005]
  Origin = -> Origin013
  Tip = -> Pad013
FEATURE [Sketcher::SketchObject] Sketch035
  FullyConstrained = true
  MapMode = 5
  Support = -> [XY_Plane007]
  expr: Constraints[19] = 22.18 * 2
  expr: Constraints[20] = dd.ddDistanceHexagono
  sketch-geometry (8):
    g0: LineSegment StartX=9.01244 StartY=15.61 StartZ=0 EndX=-9.01244 EndY=15.61 EndZ=0
    g1: LineSegment StartX=-9.01244 StartY=15.61 StartZ=0 EndX=-18.0249 EndY=-1.8e-15 EndZ=0
    g2: LineSegment StartX=-18.0249 StartY=-1.8e-15 StartZ=0 EndX=-9.01244 EndY=-15.61 EndZ=0
    g3: LineSegment StartX=-9.01244 StartY=-15.61 StartZ=0 EndX=9.01244 EndY=-15.61 EndZ=0
    g4: LineSegment StartX=9.01244 StartY=-15.61 StartZ=0 EndX=18.0249 EndY=0 EndZ=0
    g5: LineSegment StartX=18.0249 StartY=0 StartZ=0 EndX=9.01244 EndY=15.61 EndZ=0
    g6: Circle CenterX=0 CenterY=0 CenterZ=0 NormalX=0 NormalY=0 NormalZ=1 AngleXU=0 Radius=18.0249
    g7: Circle CenterX=0 CenterY=0 CenterZ=0 NormalX=0 NormalY=0 NormalZ=1 AngleXU=0 Radius=22.18
  constraints (18):
    c: Coincident(g0,g1)
    c: Coincident(g1,g2)
    c: Coincident(g2,g3)
    c: Coincident(g3,g4)
    c: Coincident(g4,g5)
    c: Coincident(g5,g0)
    c: Equal(g0, g1-g5) x5
    c: PointOnObject(g0,g6)
    c: PointOnObject(g1,g6)
    c: PointOnObject(g2,g6)
    c: PointOnObject(g3,g6)
    c: PointOnObject(g4,g6)
    c: PointOnObject(g5,g6)
    c: Coincident(g6,g-1)
    c: Coincident(g7,g6)
    c: Diameter(g7) = 44.36
    c: Distance(g1,g0) = 31.22
    c: PointOnObject(g4,g-1)
FEATURE [PartDesign::Pad] Pad014
  Direction = (0,0,1)
  Length = 16
  Length2 = 10
  Profile = -> Sketch035
  Type = 0
FEATURE [PartDesign::CoordinateSystem] LCS_separador_entrada001  label="LCS_separador_inicial_entrada001"
  AttacherType = Attacher::AttachEngine3D
  MapMode = 11
  Placement = pos=(-3.6e-15,0,0) rot=(0,0,1;1.5708rad)
  Support = -> [Pad014]
FEATURE [PartDesign::CoordinateSystem] LCS_separador_inicial_salida001
  AttacherType = Attacher::AttachEngine3D
  MapMode = 11
  Placement = pos=(-3.6e-15,0,16) rot=(0,0,1;1.5708rad)
  Support = -> [Pad014]
FEATURE [PartDesign::Body] Body014  label="SeparadorCuchillaFinal"
  Group = -> [Sketch035,Pad014,LCS_separador_entrada001,LCS_separador_inicial_salida001]
  Origin = -> Origin014
  Tip = -> Pad014
FEATURE [TechDraw::DrawSVGTemplate] Template
  EditableTexts = Designed_by_Name=Wolfang Torres; Drawing_number=PO-01-001; FC-Date=07/08/23; FC-SC=1:2; FC-SH=01; FC-Title=Cuchillas; Subtitle=Maquina de Reciclaje de Plastico; Weight=-
  Height = 210
  Orientation = 1
  Width = 297
FEATURE [TechDraw::DrawProjGroupItem] ProjItem  label="Tipo 1"
  CoarseView = false
  Direction = (0,0,1)
  Focus = 100
  HardHidden = false
  IsoCount = 0
  IsoHidden = false
  IsoVisible = false
  LockPosition = true
  Perspective = false
  Rotation = 0
  RotationVector = (1,0,0)
  Scale = 0.5
  ScaleType = 2
  ScrubCount = 0
  SeamHidden = false
  SeamVisible = true
  SmoothHidden = false
  SmoothVisible = true
  Source = -> [Body001]
  Type = 0
  X = 0
  XDirection = (1,0,0)
  Y = 0
FEATURE [TechDraw::DrawProjGroup] ProjGroup
  Anchor = -> ProjItem
  AutoDistribute = true
  LockPosition = false
  ProjectionType = 0
  Rotation = 0
  Scale = 0.5
  ScaleType = 2
  Source = -> [Body001]
  Views = -> [ProjItem]
  X = 47.3835
  Y = 166.975
  spacingX = 15
  spacingY = 15
FEATURE [TechDraw::DrawProjGroupItem] ProjItem001  label="Tipo 2"
  CoarseView = false
  Direction = (0,0,1)
  Focus = 100
  HardHidden = false
  IsoCount = 0
  IsoHidden = false
  IsoVisible = false
  LockPosition = true
  Perspective = false
  Rotation = 0
  RotationVector = (1,0,0)
  Scale = 0.5
  ScaleType = 2
  ScrubCount = 0
  SeamHidden = false
  SeamVisible = true
  SmoothHidden = false
  SmoothVisible = true
  Source = -> [Body009]
  Type = 0
  X = 0
  XDirection = (1,0,0)
  Y = 0
FEATURE [TechDraw::DrawProjGroup] ProjGroup001
  Anchor = -> ProjItem001
  AutoDistribute = true
  LockPosition = false
  ProjectionType = 0
  Rotation = 0
  Scale = 0.5
  ScaleType = 2
  Source = -> [Body009]
  Views = -> [ProjItem001]
  X = 106.926
  Y = 166.902
  spacingX = 15
  spacingY = 15
FEATURE [TechDraw::DrawProjGroupItem] ProjItem002  label="Tipo 3"
  CoarseView = false
  Direction = (0,0,1)
  Focus = 100
  HardHidden = false
  IsoCount = 0
  IsoHidden = false
  IsoVisible = false
  LockPosition = true
  Perspective = false
  Rotation = 0
  RotationVector = (1,0,0)
  Scale = 0.5
  ScaleType = 2
  ScrubCount = 0
  SeamHidden = false
  SeamVisible = true
  SmoothHidden = false
  SmoothVisible = true
  Source = -> [Body010]
  Type = 0
  X = 0
  XDirection = (1,0,0)
  Y = 0
FEATURE [TechDraw::DrawProjGroup] ProjGroup002
  Anchor = -> ProjItem002
  AutoDistribute = true
  LockPosition = false
  ProjectionType = 0
  Rotation = 0
  Scale = 0.5
  ScaleType = 2
  Source = -> [Body010]
  Views = -> [ProjItem002]
  X = 165.331
  Y = 167.204
  spacingX = 15
  spacingY = 15
FEATURE [TechDraw::DrawProjGroupItem] ProjItem003  label="Tipo 4"
  CoarseView = false
  Direction = (0,0,1)
  Focus = 100
  HardHidden = false
  IsoCount = 0
  IsoHidden = false
  IsoVisible = false
  LockPosition = true
  Perspective = false
  Rotation = 0
  RotationVector = (1,0,0)
  Scale = 0.5
  ScaleType = 2
  ScrubCount = 0
  SeamHidden = false
  SeamVisible = true
  SmoothHidden = false
  SmoothVisible = true
  Source = -> [Body011]
  Type = 0
  X = 0
  XDirection = (1,0,0)
  Y = 0
FEATURE [TechDraw::DrawProjGroup] ProjGroup003
  Anchor = -> ProjItem003
  AutoDistribute = true
  LockPosition = false
  ProjectionType = 0
  Rotation = 0
  Scale = 0.5
  ScaleType = 2
  Source = -> [Body011]
  Views = -> [ProjItem003]
  X = 47.1585
  Y = 95.6956
  spacingX = 15
  spacingY = 15
FEATURE [TechDraw::DrawProjGroupItem] ProjItem004  label="Tipo 5"
  CoarseView = false
  Direction = (0,0,1)
  Focus = 100
  HardHidden = false
  IsoCount = 0
  IsoHidden = false
  IsoVisible = false
  LockPosition = true
  Perspective = false
  Rotation = 0
  RotationVector = (1,0,0)
  Scale = 0.5
  ScaleType = 2
  ScrubCount = 0
  SeamHidden = false
  SeamVisible = true
  SmoothHidden = false
  SmoothVisible = true
  Source = -> [Body012]
  Type = 0
  X = 0
  XDirection = (1,0,0)
  Y = 0
FEATURE [TechDraw::DrawProjGroup] ProjGroup004
  Anchor = -> ProjItem004
  AutoDistribute = true
  LockPosition = false
  ProjectionType = 0
  Rotation = 0
  Scale = 0.5
  ScaleType = 2
  Source = -> [Body012]
  Views = -> [ProjItem004]
  X = 106.775
  Y = 95.7297
  spacingX = 15
  spacingY = 15
FEATURE [TechDraw::DrawProjGroupItem] ProjItem005  label="Tipo 6"
  CoarseView = false
  Direction = (0,0,1)
  Focus = 100
  HardHidden = false
  IsoCount = 0
  IsoHidden = false
  IsoVisible = false
  LockPosition = true
  Perspective = false
  Rotation = 0
  RotationVector = (1,0,0)
  Scale = 0.5
  ScaleType = 2
  ScrubCount = 0
  SeamHidden = false
  SeamVisible = true
  SmoothHidden = false
  SmoothVisible = true
  Source = -> [Body013]
  Type = 0
  X = 0
  XDirection = (1,0,0)
  Y = 0
FEATURE [TechDraw::DrawProjGroup] ProjGroup005
  Anchor = -> ProjItem005
  AutoDistribute = true
  LockPosition = false
  ProjectionType = 0
  Rotation = 0
  Scale = 0.5
  ScaleType = 2
  Source = -> [Body013]
  Views = -> [ProjItem005]
  X = 165.435
  Y = 96.07
  spacingX = 15
  spacingY = 15
FEATURE [TechDraw::DrawProjGroupItem] ProjItem006  label="Front"
  CoarseView = false
  Direction = (0,0,1)
  Focus = 100
  HardHidden = false
  IsoCount = 0
  IsoHidden = false
  IsoVisible = false
  LockPosition = true
  Perspective = false
  Rotation = 0
  RotationVector = (1,0,0)
  Scale = 0.5
  ScaleType = 2
  ScrubCount = 0
  SeamHidden = false
  SeamVisible = true
  SmoothHidden = false
  SmoothVisible = true
  Source = -> [Body001]
  Type = 0
  X = 0
  XDirection = (1,0,0)
  Y = 0
FEATURE [TechDraw::DrawViewDimension] Dimension001
  AngleOverride = false
  Arbitrary = false
  ArbitraryTolerances = false
  EqualTolerance = true
  ExtensionAngle = 0
  FormatSpec = %.2f
  FormatSpecOverTolerance = %+.2f
  FormatSpecUnderTolerance = %+.2f
  Inverted = false
  LineAngle = 0
  LockPosition = false
  MeasureType = 1
  OverTolerance = 0
  References2D = -> [ProjItem006]
  Rotation = 0
  ScaleType = 0
  TheoreticalExact = false
  Type = 1
  UnderTolerance = 0
  X = 10.7458
  Y = 18.1973
FEATURE [TechDraw::DrawViewDimension] Dimension002
  AngleOverride = false
  Arbitrary = false
  ArbitraryTolerances = false
  EqualTolerance = true
  ExtensionAngle = 0
  FormatSpec = R%.2f
  FormatSpecOverTolerance = %+.2f
  FormatSpecUnderTolerance = %+.2f
  Inverted = false
  LineAngle = 0
  LockPosition = false
  MeasureType = 1
  OverTolerance = 0
  References2D = -> [ProjItem006]
  Rotation = 0
  ScaleType = 0
  TheoreticalExact = false
  Type = 4
  UnderTolerance = 0
  X = 39.4783
  Y = 12.7745
FEATURE [TechDraw::DrawViewDimension] Dimension003
  AngleOverride = false
  Arbitrary = false
  ArbitraryTolerances = false
  EqualTolerance = true
  ExtensionAngle = 0
  FormatSpec = R%.2f
  FormatSpecOverTolerance = %+.2f
  FormatSpecUnderTolerance = %+.2f
  Inverted = false
  LineAngle = 0
  LockPosition = false
  MeasureType = 1
  OverTolerance = 0
  References2D = -> [ProjItem006]
  Rotation = 0
  ScaleType = 0
  TheoreticalExact = false
  Type = 4
  UnderTolerance = 0
  X = -25.4506
  Y = -24.1272
FEATURE [TechDraw::DrawViewDimension] Dimension004
  AngleOverride = false
  Arbitrary = false
  ArbitraryTolerances = false
  EqualTolerance = true
  ExtensionAngle = 0
  FormatSpec = %.2f
  FormatSpecOverTolerance = %+.2f
  FormatSpecUnderTolerance = %+.2f
  Inverted = false
  LineAngle = 0
  LockPosition = false
  MeasureType = 1
  OverTolerance = 0
  References2D = -> [ProjItem]
  Rotation = 0
  ScaleType = 0
  TheoreticalExact = false
  Type = 6
  UnderTolerance = 0
  X = 2.86423
  Y = -12.3556
FEATURE [TechDraw::DrawViewDimension] Dimension005
  AngleOverride = false
  Arbitrary = false
  ArbitraryTolerances = false
  EqualTolerance = true
  ExtensionAngle = 0
  FormatSpec = %.2f
  FormatSpecOverTolerance = %+.2f
  FormatSpecUnderTolerance = %+.2f
  Inverted = false
  LineAngle = 0
  LockPosition = false
  MeasureType = 1
  OverTolerance = 0
  References2D = -> [ProjItem001]
  Rotation = 0
  ScaleType = 0
  TheoreticalExact = false
  Type = 6
  UnderTolerance = 0
  X = 0.374085
  Y = -13.4002
FEATURE [TechDraw::DrawViewDimension] Dimension006
  AngleOverride = false
  Arbitrary = false
  ArbitraryTolerances = false
  EqualTolerance = true
  ExtensionAngle = 0
  FormatSpec = %.2f
  FormatSpecOverTolerance = %+.2f
  FormatSpecUnderTolerance = %+.2f
  Inverted = false
  LineAngle = 0
  LockPosition = false
  MeasureType = 1
  OverTolerance = 0
  References2D = -> [ProjItem002]
  Rotation = 0
  ScaleType = 0
  TheoreticalExact = false
  Type = 6
  UnderTolerance = 0
  X = -0.120951
  Y = -12.7489
FEATURE [TechDraw::DrawViewDimension] Dimension007
  AngleOverride = false
  Arbitrary = false
  ArbitraryTolerances = false
  EqualTolerance = true
  ExtensionAngle = 0
  FormatSpec = %.2f
  FormatSpecOverTolerance = %+.2f
  FormatSpecUnderTolerance = %+.2f
  Inverted = false
  LineAngle = 0
  LockPosition = false
  MeasureType = 1
  OverTolerance = 0
  References2D = -> [ProjItem005]
  Rotation = 0
  ScaleType = 0
  TheoreticalExact = false
  Type = 6
  UnderTolerance = 0
  X = 1.91677
  Y = -12.1832
FEATURE [TechDraw::DrawViewDimension] Dimension008
  AngleOverride = false
  Arbitrary = false
  ArbitraryTolerances = false
  EqualTolerance = true
  ExtensionAngle = 0
  FormatSpec = %.2f
  FormatSpecOverTolerance = %+.2f
  FormatSpecUnderTolerance = %+.2f
  Inverted = false
  LineAngle = 0
  LockPosition = false
  MeasureType = 1
  OverTolerance = 0
  References2D = -> [ProjItem004]
  Rotation = 0
  ScaleType = 0
  TheoreticalExact = false
  Type = 6
  UnderTolerance = 0
  X = 2.97494
  Y = -12.2998
FEATURE [TechDraw::DrawViewDimension] Dimension009
  AngleOverride = false
  Arbitrary = false
  ArbitraryTolerances = false
  EqualTolerance = true
  ExtensionAngle = 0
  FormatSpec = %.2f
  FormatSpecOverTolerance = %+.2f
  FormatSpecUnderTolerance = %+.2f
  Inverted = false
  LineAngle = 0
  LockPosition = false
  MeasureType = 1
  OverTolerance = 0
  References2D = -> [ProjItem003]
  Rotation = 0
  ScaleType = 0
  TheoreticalExact = false
  Type = 6
  UnderTolerance = 0
  X = 0.821844
  Y = -13.0254
FEATURE [TechDraw::DrawProjGroupItem] ProjItem008  label="Bottom"
  CoarseView = false
  Direction = (0,-1,0)
  Focus = 100
  HardHidden = false
  IsoCount = 0
  IsoHidden = false
  IsoVisible = false
  LockPosition = false
  Perspective = false
  Rotation = 0
  RotationVector = (1,0,0)
  ScaleType = 2
  ScrubCount = 0
  SeamHidden = false
  SeamVisible = true
  SmoothHidden = false
  SmoothVisible = true
  Source = -> [Body001]
  Type = 5
  X = 0
  XDirection = (1,0,0)
  Y = 39.5608
FEATURE [TechDraw::DrawProjGroup] ProjGroup006
  Anchor = -> ProjItem006
  AutoDistribute = true
  LockPosition = false
  ProjectionType = 0
  Rotation = 0
  Scale = 0.5
  ScaleType = 2
  Source = -> [Body001]
  Views = -> [ProjItem006,ProjItem008]
  X = 236.644
  Y = 96.1298
  spacingX = 15
  spacingY = 15
FEATURE [TechDraw::DrawViewDimension] Dimension010
  AngleOverride = false
  Arbitrary = false
  ArbitraryTolerances = false
  EqualTolerance = true
  ExtensionAngle = 0
  FormatSpec = %.2w
  FormatSpecOverTolerance = %+.2w
  FormatSpecUnderTolerance = %+.2w
  Inverted = false
  LineAngle = 0
  LockPosition = false
  MeasureType = 1
  OverTolerance = 0
  References2D = -> [ProjItem008]
  Rotation = 0
  ScaleType = 0
  TheoreticalExact = false
  Type = 1
  UnderTolerance = 0
  X = 0.934532
  Y = 13.1549
FEATURE [TechDraw::DrawViewDimension] Dimension011
  AngleOverride = false
  Arbitrary = false
  ArbitraryTolerances = false
  EqualTolerance = true
  ExtensionAngle = 0
  FormatSpec = ⌀%.2w
  FormatSpecOverTolerance = %+.2w
  FormatSpecUnderTolerance = %+.2w
  Inverted = false
  LineAngle = 0
  LockPosition = false
  MeasureType = 1
  OverTolerance = 0
  References2D = -> [ProjItem006]
  Rotation = 0
  ScaleType = 0
  TheoreticalExact = false
  Type = 5
  UnderTolerance = 0
  X = -32.9302
  Y = 11.5325
FEATURE [TechDraw::DrawViewDimension] Dimension012
  AngleOverride = false
  Arbitrary = false
  ArbitraryTolerances = false
  EqualTolerance = true
  ExtensionAngle = 0
  FormatSpec = ⌀%.2w
  FormatSpecOverTolerance = %+.2w
  FormatSpecUnderTolerance = %+.2w
  Inverted = false
  LineAngle = 0
  LockPosition = false
  MeasureType = 1
  OverTolerance = 0
  References2D = -> [ProjItem006]
  Rotation = 0
  ScaleType = 0
  TheoreticalExact = false
  Type = 5
  UnderTolerance = 0
  X = -26.1218
  Y = 26.9555
FEATURE [TechDraw::DrawViewDimension] Dimension
  AngleOverride = false
  Arbitrary = false
  ArbitraryTolerances = false
  EqualTolerance = true
  ExtensionAngle = 0
  FormatSpec = %.2w
  FormatSpecOverTolerance = %+.2w
  FormatSpecUnderTolerance = %+.2w
  Inverted = false
  LineAngle = 0
  LockPosition = false
  MeasureType = 1
  OverTolerance = 0
  References2D = -> [ProjItem008]
  Rotation = 0
  ScaleType = 0
  TheoreticalExact = false
  Type = 2
  UnderTolerance = 0
  X = 33.8651
  Y = 10.9696
FEATURE [TechDraw::DrawPage] Page
  KeepUpdated = true
  NextBalloonIndex = 1
  ProjectionType = 0
  Template = -> Template
  Views = -> [ProjGroup,ProjGroup001,ProjGroup002,ProjGroup003,ProjGroup004,ProjGroup005,ProjGroup006,Dimension001,Dimension002,Dimension003,Dimension004,Dimension005,Dimension006,Dimension007,Dimension008,Dimension009,Dimension010,Dimension011,Dimension012,Dimension]
